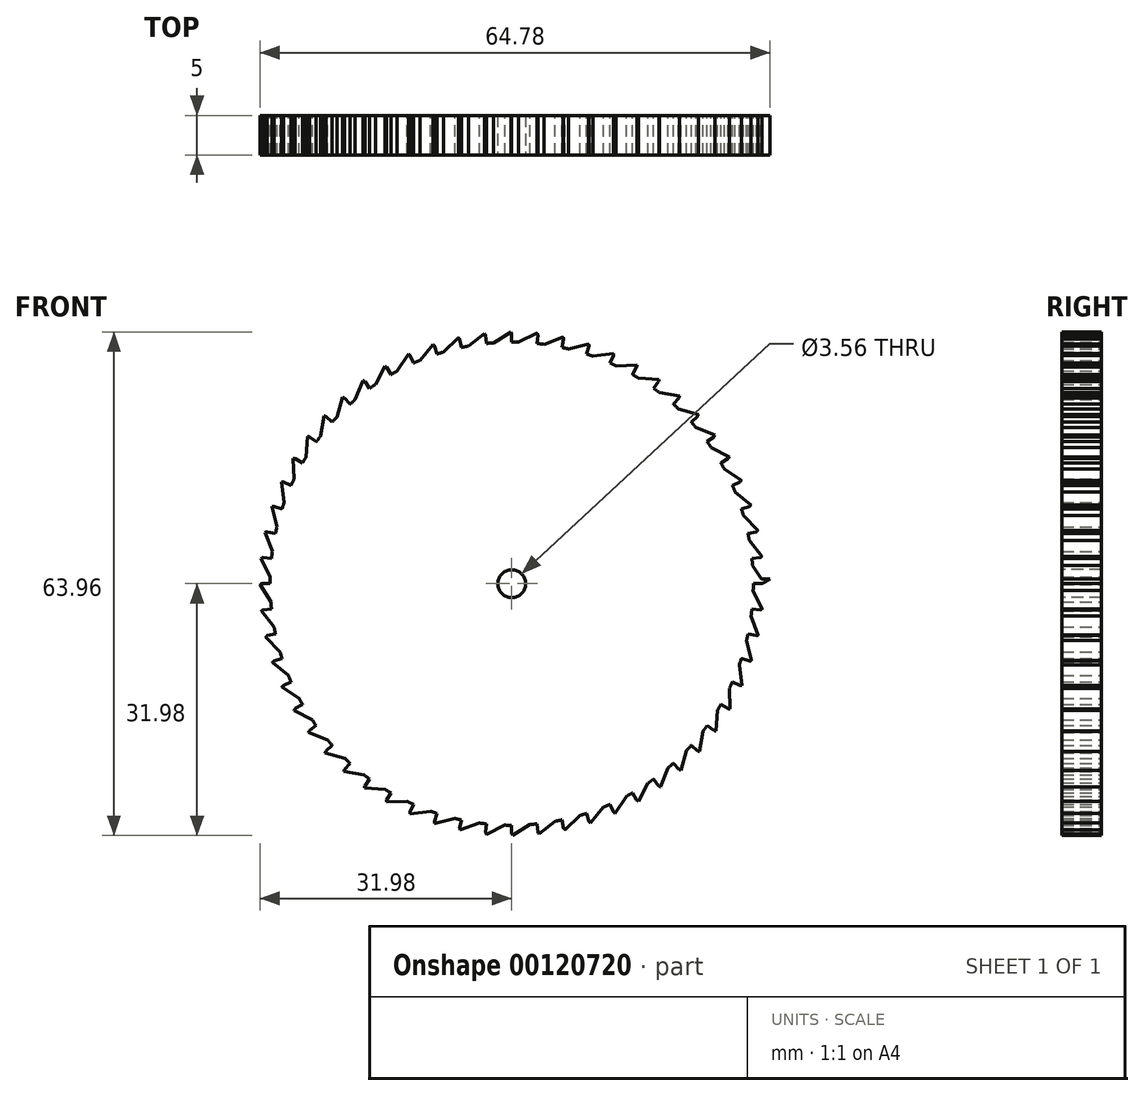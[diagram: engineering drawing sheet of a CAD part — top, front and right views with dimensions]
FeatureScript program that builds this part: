
annotation { "Feature Type Name" : "Feature", "Feature Type Description" : "" }
export const myFeature = defineFeature(function(context is Context, id is Id, definition is map)
    precondition{}
    {
        {
            var Q0;
            Q0=qCreatedBy(makeId("Front.planeOp"),FACE);
            var sketch = newSketch(context, id + "F0", { "sketchPlane" : qUnion([Q0])});
            skArc(sketch, "E0", {"start": v(-7.94, 29.64) * mm, "mid": v(-8.71, 29.42) * mm, "end": v(-9.48, 29.18) * mm});
            skArc(sketch, "E1.trimOffspring", {"start": v(0, 31.75) * mm, "mid": v(-0.28, 32.29) * mm, "end": v(-0.6, 32.8) * mm});
            skLineSegment(sketch, "E2", {"start": v(0, 31.75) * mm, "end": v(0, 30.68) * mm});
            skLineSegment(sketch, "E3", {"start": v(-0.6, 32.8) * mm, "end": v(-0.86, 32.8) * mm});
            skLineSegment(sketch, "E4.MirrorCS", {"start": v(-0.73, 27.19) * mm, "end": v(17.28, 27.8) * mm});
            skArc(sketch, "E5.MirrorCS", {"start": v(-1.66, 31.7) * mm, "mid": v(-1.4, 32.26) * mm, "end": v(-1.12, 32.79) * mm});
            skLineSegment(sketch, "E6.MirrorCS", {"start": v(-1.66, 31.7) * mm, "end": v(-1.6, 30.64) * mm});
            skLineSegment(sketch, "E7.1.0", {"start": v(-4.97, 31.36) * mm, "end": v(-4.8, 30.3) * mm});
            skArc(sketch, "E7.1.1", {"start": v(-4.97, 31.36) * mm, "mid": v(-4.77, 31.93) * mm, "end": v(-4.54, 32.49) * mm});
            skLineSegment(sketch, "E7.1.2", {"start": v(-3.57, 26.96) * mm, "end": v(14.28, 29.45) * mm});
            skLineSegment(sketch, "E7.1.3", {"start": v(-4.03, 32.56) * mm, "end": v(-4.28, 32.52) * mm});
            skArc(sketch, "E7.1.4", {"start": v(-3.32, 31.58) * mm, "mid": v(-3.65, 32.08) * mm, "end": v(-4.03, 32.56) * mm});
            skLineSegment(sketch, "E7.1.5", {"start": v(-3.32, 31.58) * mm, "end": v(-3.2, 30.52) * mm});
            skLineSegment(sketch, "E7.2.0", {"start": v(-8.22, 30.67) * mm, "end": v(-7.94, 29.64) * mm});
            skArc(sketch, "E7.2.1", {"start": v(-8.22, 30.67) * mm, "mid": v(-8.08, 31.26) * mm, "end": v(-7.9, 31.84) * mm});
            skLineSegment(sketch, "E7.2.2", {"start": v(-6.37, 26.44) * mm, "end": v(11.12, 30.78) * mm});
            skLineSegment(sketch, "E7.2.3", {"start": v(-7.4, 31.96) * mm, "end": v(-7.66, 31.9) * mm});
            skArc(sketch, "E7.2.4", {"start": v(-6.6, 31.06) * mm, "mid": v(-6.99, 31.52) * mm, "end": v(-7.4, 31.96) * mm});
            skLineSegment(sketch, "E7.2.5", {"start": v(-6.6, 31.06) * mm, "end": v(-6.38, 30.01) * mm});
            skLineSegment(sketch, "E7.3.0", {"start": v(-11.38, 29.64) * mm, "end": v(-11, 28.65) * mm});
            skArc(sketch, "E7.3.1", {"start": v(-11.38, 29.64) * mm, "mid": v(-11.3, 30.24) * mm, "end": v(-11.2, 30.84) * mm});
            skLineSegment(sketch, "E7.3.2", {"start": v(-9.1, 25.63) * mm, "end": v(7.84, 31.78) * mm});
            skLineSegment(sketch, "E7.3.3", {"start": v(-10.7, 31) * mm, "end": v(-10.95, 30.92) * mm});
            skArc(sketch, "E7.3.4", {"start": v(-9.81, 30.2) * mm, "mid": v(-10.24, 30.62) * mm, "end": v(-10.7, 31) * mm});
            skLineSegment(sketch, "E7.3.5", {"start": v(-9.81, 30.2) * mm, "end": v(-9.48, 29.18) * mm});
            skLineSegment(sketch, "E7.4.0", {"start": v(-14.41, 28.29) * mm, "end": v(-13.93, 27.34) * mm});
            skArc(sketch, "E7.4.1", {"start": v(-14.41, 28.29) * mm, "mid": v(-14.4, 28.9) * mm, "end": v(-14.35, 29.5) * mm});
            skLineSegment(sketch, "E7.4.2", {"start": v(-11.73, 24.54) * mm, "end": v(4.48, 32.42) * mm});
            skLineSegment(sketch, "E7.4.3", {"start": v(-13.9, 29.72) * mm, "end": v(-14.12, 29.6) * mm});
            skArc(sketch, "E7.4.4", {"start": v(-12.91, 29) * mm, "mid": v(-13.39, 29.38) * mm, "end": v(-13.9, 29.72) * mm});
            skLineSegment(sketch, "E7.4.5", {"start": v(-12.91, 29) * mm, "end": v(-12.48, 28.03) * mm});
            skLineSegment(sketch, "E7.5.0", {"start": v(-17.3, 26.63) * mm, "end": v(-16.71, 25.73) * mm});
            skArc(sketch, "E7.5.1", {"start": v(-17.3, 26.63) * mm, "mid": v(-17.35, 27.23) * mm, "end": v(-17.36, 27.84) * mm});
            skLineSegment(sketch, "E7.5.2", {"start": v(-14.23, 23.18) * mm, "end": v(1.07, 32.72) * mm});
            skLineSegment(sketch, "E7.5.3", {"start": v(-16.92, 28.1) * mm, "end": v(-17.14, 27.97) * mm});
            skArc(sketch, "E7.5.4", {"start": v(-15.88, 27.5) * mm, "mid": v(-16.39, 27.82) * mm, "end": v(-16.92, 28.1) * mm});
            skLineSegment(sketch, "E7.5.5", {"start": v(-15.87, 27.5) * mm, "end": v(-15.34, 26.57) * mm});
            skLineSegment(sketch, "E7.6.0", {"start": v(-19.98, 24.67) * mm, "end": v(-19.3, 23.85) * mm});
            skArc(sketch, "E7.6.1", {"start": v(-19.98, 24.67) * mm, "mid": v(-20.1, 25.27) * mm, "end": v(-20.17, 25.87) * mm});
            skLineSegment(sketch, "E7.6.2", {"start": v(-16.57, 21.56) * mm, "end": v(-2.36, 32.65) * mm});
            skLineSegment(sketch, "E7.6.3", {"start": v(-19.77, 26.18) * mm, "end": v(-19.97, 26.03) * mm});
            skArc(sketch, "E7.6.4", {"start": v(-18.66, 25.69) * mm, "mid": v(-19.2, 25.95) * mm, "end": v(-19.77, 26.18) * mm});
            skLineSegment(sketch, "E7.6.5", {"start": v(-18.66, 25.69) * mm, "end": v(-18.04, 24.82) * mm});
            skLineSegment(sketch, "E7.7.0", {"start": v(-22.45, 22.45) * mm, "end": v(-21.7, 21.7) * mm});
            skArc(sketch, "E7.7.1", {"start": v(-22.45, 22.45) * mm, "mid": v(-22.63, 23.03) * mm, "end": v(-22.77, 23.62) * mm});
            skLineSegment(sketch, "E7.7.2", {"start": v(-18.74, 19.71) * mm, "end": v(-5.76, 32.22) * mm});
            skLineSegment(sketch, "E7.7.3", {"start": v(-22.4, 23.97) * mm, "end": v(-22.58, 23.8) * mm});
            skArc(sketch, "E7.7.4", {"start": v(-21.24, 23.6) * mm, "mid": v(-21.81, 23.8) * mm, "end": v(-22.4, 23.97) * mm});
            skLineSegment(sketch, "E7.7.5", {"start": v(-21.24, 23.6) * mm, "end": v(-20.53, 22.8) * mm});
            skLineSegment(sketch, "E7.8.0", {"start": v(-24.67, 19.98) * mm, "end": v(-23.85, 19.3) * mm});
            skArc(sketch, "E7.8.1", {"start": v(-24.67, 19.98) * mm, "mid": v(-24.91, 20.54) * mm, "end": v(-25.11, 21.1) * mm});
            skLineSegment(sketch, "E7.8.2", {"start": v(-20.7, 17.65) * mm, "end": v(-9.1, 31.44) * mm});
            skLineSegment(sketch, "E7.8.3", {"start": v(-24.78, 21.5) * mm, "end": v(-24.95, 21.3) * mm});
            skArc(sketch, "E7.8.4", {"start": v(-23.6, 21.24) * mm, "mid": v(-24.18, 21.4) * mm, "end": v(-24.78, 21.5) * mm});
            skLineSegment(sketch, "E7.8.5", {"start": v(-23.6, 21.24) * mm, "end": v(-22.8, 20.53) * mm});
            skLineSegment(sketch, "E7.9.0", {"start": v(-26.63, 17.3) * mm, "end": v(-25.73, 16.71) * mm});
            skArc(sketch, "E7.9.1", {"start": v(-26.63, 17.3) * mm, "mid": v(-26.92, 17.82) * mm, "end": v(-27.18, 18.37) * mm});
            skLineSegment(sketch, "E7.9.2", {"start": v(-22.43, 15.39) * mm, "end": v(-12.33, 30.32) * mm});
            skLineSegment(sketch, "E7.9.3", {"start": v(-26.89, 18.8) * mm, "end": v(-27.04, 18.58) * mm});
            skArc(sketch, "E7.9.4", {"start": v(-25.69, 18.66) * mm, "mid": v(-26.28, 18.75) * mm, "end": v(-26.89, 18.8) * mm});
            skLineSegment(sketch, "E7.9.5", {"start": v(-25.69, 18.66) * mm, "end": v(-24.82, 18.04) * mm});
            skLineSegment(sketch, "E7.10.0", {"start": v(-28.29, 14.41) * mm, "end": v(-27.34, 13.93) * mm});
            skArc(sketch, "E7.10.1", {"start": v(-28.29, 14.41) * mm, "mid": v(-28.64, 14.9) * mm, "end": v(-28.95, 15.43) * mm});
            skLineSegment(sketch, "E7.10.2", {"start": v(-23.91, 12.96) * mm, "end": v(-15.43, 28.87) * mm});
            skLineSegment(sketch, "E7.10.3", {"start": v(-28.7, 15.88) * mm, "end": v(-28.83, 15.65) * mm});
            skArc(sketch, "E7.10.4", {"start": v(-27.5, 15.88) * mm, "mid": v(-28.1, 15.9) * mm, "end": v(-28.7, 15.88) * mm});
            skLineSegment(sketch, "E7.10.5", {"start": v(-27.5, 15.88) * mm, "end": v(-26.57, 15.34) * mm});
            skLineSegment(sketch, "E7.11.0", {"start": v(-29.64, 11.38) * mm, "end": v(-28.65, 11) * mm});
            skArc(sketch, "E7.11.1", {"start": v(-29.64, 11.38) * mm, "mid": v(-30.04, 11.83) * mm, "end": v(-30.4, 12.32) * mm});
            skLineSegment(sketch, "E7.11.2", {"start": v(-25.13, 10.39) * mm, "end": v(-18.37, 27.1) * mm});
            skLineSegment(sketch, "E7.11.3", {"start": v(-30.2, 12.8) * mm, "end": v(-30.3, 12.55) * mm});
            skArc(sketch, "E7.11.4", {"start": v(-29, 12.91) * mm, "mid": v(-29.6, 12.88) * mm, "end": v(-30.2, 12.8) * mm});
            skLineSegment(sketch, "E7.11.5", {"start": v(-29, 12.91) * mm, "end": v(-28.03, 12.48) * mm});
            skLineSegment(sketch, "E7.12.0", {"start": v(-30.67, 8.22) * mm, "end": v(-29.64, 7.94) * mm});
            skArc(sketch, "E7.12.1", {"start": v(-30.67, 8.22) * mm, "mid": v(-31.11, 8.63) * mm, "end": v(-31.53, 9.07) * mm});
            skLineSegment(sketch, "E7.12.2", {"start": v(-26.08, 7.7) * mm, "end": v(-21.1, 25.03) * mm});
            skLineSegment(sketch, "E7.12.3", {"start": v(-31.38, 9.56) * mm, "end": v(-31.45, 9.32) * mm});
            skArc(sketch, "E7.12.4", {"start": v(-30.2, 9.81) * mm, "mid": v(-30.8, 9.7) * mm, "end": v(-31.38, 9.56) * mm});
            skLineSegment(sketch, "E7.12.5", {"start": v(-30.2, 9.81) * mm, "end": v(-29.18, 9.48) * mm});
            skLineSegment(sketch, "E7.13.0", {"start": v(-31.36, 4.97) * mm, "end": v(-30.3, 4.8) * mm});
            skArc(sketch, "E7.13.1", {"start": v(-31.36, 4.97) * mm, "mid": v(-31.84, 5.33) * mm, "end": v(-32.3, 5.73) * mm});
            skLineSegment(sketch, "E7.13.2", {"start": v(-26.75, 4.93) * mm, "end": v(-23.6, 22.68) * mm});
            skLineSegment(sketch, "E7.13.3", {"start": v(-32.2, 6.23) * mm, "end": v(-32.26, 5.98) * mm});
            skArc(sketch, "E7.13.4", {"start": v(-31.06, 6.6) * mm, "mid": v(-31.64, 6.44) * mm, "end": v(-32.2, 6.23) * mm});
            skLineSegment(sketch, "E7.13.5", {"start": v(-31.06, 6.6) * mm, "end": v(-30.01, 6.38) * mm});
            skLineSegment(sketch, "E7.14.0", {"start": v(-31.7, 1.66) * mm, "end": v(-30.64, 1.6) * mm});
            skArc(sketch, "E7.14.1", {"start": v(-31.7, 1.66) * mm, "mid": v(-32.23, 1.97) * mm, "end": v(-32.72, 2.32) * mm});
            skLineSegment(sketch, "E7.14.2", {"start": v(-27.11, 2.11) * mm, "end": v(-25.84, 20.1) * mm});
            skLineSegment(sketch, "E7.14.3", {"start": v(-32.68, 2.83) * mm, "end": v(-32.7, 2.57) * mm});
            skArc(sketch, "E7.14.4", {"start": v(-31.58, 3.32) * mm, "mid": v(-32.14, 3.1) * mm, "end": v(-32.68, 2.83) * mm});
            skLineSegment(sketch, "E7.14.5", {"start": v(-31.58, 3.32) * mm, "end": v(-30.52, 3.2) * mm});
            skLineSegment(sketch, "E7.15.0", {"start": v(-31.7, -1.66) * mm, "end": v(-30.64, -1.6) * mm});
            skArc(sketch, "E7.15.1", {"start": v(-31.7, -1.66) * mm, "mid": v(-32.26, -1.4) * mm, "end": v(-32.79, -1.12) * mm});
            skLineSegment(sketch, "E7.15.2", {"start": v(-27.19, -0.73) * mm, "end": v(-27.8, 17.28) * mm});
            skLineSegment(sketch, "E7.15.3", {"start": v(-32.8, -0.6) * mm, "end": v(-32.8, -0.86) * mm});
            skArc(sketch, "E7.15.4", {"start": v(-31.75, 0) * mm, "mid": v(-32.29, -0.28) * mm, "end": v(-32.8, -0.6) * mm});
            skLineSegment(sketch, "E7.15.5", {"start": v(-31.75, 0) * mm, "end": v(-30.68, 0) * mm});
            skLineSegment(sketch, "E7.16.0", {"start": v(-31.36, -4.97) * mm, "end": v(-30.3, -4.8) * mm});
            skArc(sketch, "E7.16.1", {"start": v(-31.36, -4.97) * mm, "mid": v(-31.93, -4.77) * mm, "end": v(-32.49, -4.54) * mm});
            skLineSegment(sketch, "E7.16.2", {"start": v(-26.96, -3.57) * mm, "end": v(-29.45, 14.28) * mm});
            skLineSegment(sketch, "E7.16.3", {"start": v(-32.56, -4.03) * mm, "end": v(-32.52, -4.28) * mm});
            skArc(sketch, "E7.16.4", {"start": v(-31.58, -3.32) * mm, "mid": v(-32.08, -3.65) * mm, "end": v(-32.56, -4.03) * mm});
            skLineSegment(sketch, "E7.16.5", {"start": v(-31.58, -3.32) * mm, "end": v(-30.52, -3.2) * mm});
            skLineSegment(sketch, "E7.17.0", {"start": v(-30.67, -8.22) * mm, "end": v(-29.64, -7.94) * mm});
            skArc(sketch, "E7.17.1", {"start": v(-30.67, -8.22) * mm, "mid": v(-31.26, -8.08) * mm, "end": v(-31.84, -7.9) * mm});
            skLineSegment(sketch, "E7.17.2", {"start": v(-26.44, -6.37) * mm, "end": v(-30.78, 11.12) * mm});
            skLineSegment(sketch, "E7.17.3", {"start": v(-31.96, -7.4) * mm, "end": v(-31.9, -7.66) * mm});
            skArc(sketch, "E7.17.4", {"start": v(-31.06, -6.6) * mm, "mid": v(-31.52, -6.99) * mm, "end": v(-31.96, -7.4) * mm});
            skLineSegment(sketch, "E7.17.5", {"start": v(-31.06, -6.6) * mm, "end": v(-30.01, -6.38) * mm});
            skLineSegment(sketch, "E7.18.0", {"start": v(-29.64, -11.38) * mm, "end": v(-28.65, -11) * mm});
            skArc(sketch, "E7.18.1", {"start": v(-29.64, -11.38) * mm, "mid": v(-30.24, -11.3) * mm, "end": v(-30.84, -11.2) * mm});
            skLineSegment(sketch, "E7.18.2", {"start": v(-25.63, -9.1) * mm, "end": v(-31.78, 7.84) * mm});
            skLineSegment(sketch, "E7.18.3", {"start": v(-31, -10.7) * mm, "end": v(-30.92, -10.95) * mm});
            skArc(sketch, "E7.18.4", {"start": v(-30.2, -9.81) * mm, "mid": v(-30.62, -10.24) * mm, "end": v(-31, -10.7) * mm});
            skLineSegment(sketch, "E7.18.5", {"start": v(-30.2, -9.81) * mm, "end": v(-29.18, -9.48) * mm});
            skLineSegment(sketch, "E7.19.0", {"start": v(-28.29, -14.41) * mm, "end": v(-27.34, -13.93) * mm});
            skArc(sketch, "E7.19.1", {"start": v(-28.29, -14.41) * mm, "mid": v(-28.9, -14.4) * mm, "end": v(-29.5, -14.35) * mm});
            skLineSegment(sketch, "E7.19.2", {"start": v(-24.54, -11.73) * mm, "end": v(-32.42, 4.48) * mm});
            skLineSegment(sketch, "E7.19.3", {"start": v(-29.72, -13.9) * mm, "end": v(-29.6, -14.12) * mm});
            skArc(sketch, "E7.19.4", {"start": v(-29, -12.91) * mm, "mid": v(-29.38, -13.39) * mm, "end": v(-29.72, -13.9) * mm});
            skLineSegment(sketch, "E7.19.5", {"start": v(-29, -12.91) * mm, "end": v(-28.03, -12.48) * mm});
            skLineSegment(sketch, "E7.20.0", {"start": v(-26.63, -17.3) * mm, "end": v(-25.73, -16.71) * mm});
            skArc(sketch, "E7.20.1", {"start": v(-26.63, -17.3) * mm, "mid": v(-27.23, -17.35) * mm, "end": v(-27.84, -17.36) * mm});
            skLineSegment(sketch, "E7.20.2", {"start": v(-23.18, -14.23) * mm, "end": v(-32.72, 1.07) * mm});
            skLineSegment(sketch, "E7.20.3", {"start": v(-28.1, -16.92) * mm, "end": v(-27.97, -17.14) * mm});
            skArc(sketch, "E7.20.4", {"start": v(-27.5, -15.87) * mm, "mid": v(-27.82, -16.39) * mm, "end": v(-28.1, -16.92) * mm});
            skLineSegment(sketch, "E7.20.5", {"start": v(-27.5, -15.87) * mm, "end": v(-26.57, -15.34) * mm});
            skLineSegment(sketch, "E7.21.0", {"start": v(-24.67, -19.98) * mm, "end": v(-23.85, -19.3) * mm});
            skArc(sketch, "E7.21.1", {"start": v(-24.67, -19.98) * mm, "mid": v(-25.27, -20.1) * mm, "end": v(-25.87, -20.17) * mm});
            skLineSegment(sketch, "E7.21.2", {"start": v(-21.56, -16.57) * mm, "end": v(-32.65, -2.36) * mm});
            skLineSegment(sketch, "E7.21.3", {"start": v(-26.18, -19.77) * mm, "end": v(-26.03, -19.97) * mm});
            skArc(sketch, "E7.21.4", {"start": v(-25.69, -18.66) * mm, "mid": v(-25.95, -19.2) * mm, "end": v(-26.18, -19.77) * mm});
            skLineSegment(sketch, "E7.21.5", {"start": v(-25.69, -18.66) * mm, "end": v(-24.82, -18.04) * mm});
            skLineSegment(sketch, "E7.22.0", {"start": v(-22.45, -22.45) * mm, "end": v(-21.7, -21.7) * mm});
            skArc(sketch, "E7.22.1", {"start": v(-22.45, -22.45) * mm, "mid": v(-23.03, -22.63) * mm, "end": v(-23.62, -22.77) * mm});
            skLineSegment(sketch, "E7.22.2", {"start": v(-19.71, -18.74) * mm, "end": v(-32.22, -5.76) * mm});
            skLineSegment(sketch, "E7.22.3", {"start": v(-23.97, -22.4) * mm, "end": v(-23.8, -22.58) * mm});
            skArc(sketch, "E7.22.4", {"start": v(-23.6, -21.24) * mm, "mid": v(-23.8, -21.81) * mm, "end": v(-23.97, -22.4) * mm});
            skLineSegment(sketch, "E7.22.5", {"start": v(-23.6, -21.24) * mm, "end": v(-22.8, -20.53) * mm});
            skLineSegment(sketch, "E7.23.0", {"start": v(-19.98, -24.67) * mm, "end": v(-19.3, -23.85) * mm});
            skArc(sketch, "E7.23.1", {"start": v(-19.98, -24.67) * mm, "mid": v(-20.54, -24.91) * mm, "end": v(-21.1, -25.11) * mm});
            skLineSegment(sketch, "E7.23.2", {"start": v(-17.65, -20.7) * mm, "end": v(-31.44, -9.1) * mm});
            skLineSegment(sketch, "E7.23.3", {"start": v(-21.5, -24.78) * mm, "end": v(-21.3, -24.95) * mm});
            skArc(sketch, "E7.23.4", {"start": v(-21.24, -23.6) * mm, "mid": v(-21.4, -24.18) * mm, "end": v(-21.5, -24.78) * mm});
            skLineSegment(sketch, "E7.23.5", {"start": v(-21.24, -23.6) * mm, "end": v(-20.53, -22.8) * mm});
            skLineSegment(sketch, "E7.24.0", {"start": v(-17.3, -26.63) * mm, "end": v(-16.71, -25.73) * mm});
            skArc(sketch, "E7.24.1", {"start": v(-17.3, -26.63) * mm, "mid": v(-17.82, -26.92) * mm, "end": v(-18.37, -27.18) * mm});
            skLineSegment(sketch, "E7.24.2", {"start": v(-15.39, -22.43) * mm, "end": v(-30.32, -12.33) * mm});
            skLineSegment(sketch, "E7.24.3", {"start": v(-18.8, -26.89) * mm, "end": v(-18.58, -27.04) * mm});
            skArc(sketch, "E7.24.4", {"start": v(-18.66, -25.69) * mm, "mid": v(-18.75, -26.28) * mm, "end": v(-18.8, -26.89) * mm});
            skLineSegment(sketch, "E7.24.5", {"start": v(-18.66, -25.69) * mm, "end": v(-18.04, -24.82) * mm});
            skLineSegment(sketch, "E7.25.0", {"start": v(-14.41, -28.29) * mm, "end": v(-13.93, -27.34) * mm});
            skArc(sketch, "E7.25.1", {"start": v(-14.41, -28.29) * mm, "mid": v(-14.9, -28.64) * mm, "end": v(-15.43, -28.95) * mm});
            skLineSegment(sketch, "E7.25.2", {"start": v(-12.96, -23.91) * mm, "end": v(-28.87, -15.43) * mm});
            skLineSegment(sketch, "E7.25.3", {"start": v(-15.88, -28.7) * mm, "end": v(-15.65, -28.83) * mm});
            skArc(sketch, "E7.25.4", {"start": v(-15.88, -27.5) * mm, "mid": v(-15.9, -28.1) * mm, "end": v(-15.88, -28.7) * mm});
            skLineSegment(sketch, "E7.25.5", {"start": v(-15.87, -27.5) * mm, "end": v(-15.34, -26.57) * mm});
            skLineSegment(sketch, "E7.26.0", {"start": v(-11.38, -29.64) * mm, "end": v(-11, -28.65) * mm});
            skArc(sketch, "E7.26.1", {"start": v(-11.38, -29.64) * mm, "mid": v(-11.83, -30.04) * mm, "end": v(-12.32, -30.4) * mm});
            skLineSegment(sketch, "E7.26.2", {"start": v(-10.39, -25.13) * mm, "end": v(-27.1, -18.37) * mm});
            skLineSegment(sketch, "E7.26.3", {"start": v(-12.8, -30.2) * mm, "end": v(-12.55, -30.3) * mm});
            skArc(sketch, "E7.26.4", {"start": v(-12.91, -29) * mm, "mid": v(-12.88, -29.6) * mm, "end": v(-12.8, -30.2) * mm});
            skLineSegment(sketch, "E7.26.5", {"start": v(-12.91, -29) * mm, "end": v(-12.48, -28.03) * mm});
            skLineSegment(sketch, "E7.27.0", {"start": v(-8.22, -30.67) * mm, "end": v(-7.94, -29.64) * mm});
            skArc(sketch, "E7.27.1", {"start": v(-8.22, -30.67) * mm, "mid": v(-8.63, -31.11) * mm, "end": v(-9.07, -31.53) * mm});
            skLineSegment(sketch, "E7.27.2", {"start": v(-7.7, -26.08) * mm, "end": v(-25.03, -21.1) * mm});
            skLineSegment(sketch, "E7.27.3", {"start": v(-9.56, -31.38) * mm, "end": v(-9.32, -31.45) * mm});
            skArc(sketch, "E7.27.4", {"start": v(-9.81, -30.2) * mm, "mid": v(-9.7, -30.8) * mm, "end": v(-9.56, -31.38) * mm});
            skLineSegment(sketch, "E7.27.5", {"start": v(-9.81, -30.2) * mm, "end": v(-9.48, -29.18) * mm});
            skLineSegment(sketch, "E7.28.0", {"start": v(-4.97, -31.36) * mm, "end": v(-4.8, -30.3) * mm});
            skArc(sketch, "E7.28.1", {"start": v(-4.97, -31.36) * mm, "mid": v(-5.33, -31.84) * mm, "end": v(-5.73, -32.3) * mm});
            skLineSegment(sketch, "E7.28.2", {"start": v(-4.93, -26.75) * mm, "end": v(-22.68, -23.6) * mm});
            skLineSegment(sketch, "E7.28.3", {"start": v(-6.23, -32.2) * mm, "end": v(-5.98, -32.26) * mm});
            skArc(sketch, "E7.28.4", {"start": v(-6.6, -31.06) * mm, "mid": v(-6.44, -31.64) * mm, "end": v(-6.23, -32.2) * mm});
            skLineSegment(sketch, "E7.28.5", {"start": v(-6.6, -31.06) * mm, "end": v(-6.38, -30.01) * mm});
            skLineSegment(sketch, "E7.29.0", {"start": v(-1.66, -31.7) * mm, "end": v(-1.6, -30.64) * mm});
            skArc(sketch, "E7.29.1", {"start": v(-1.66, -31.7) * mm, "mid": v(-1.97, -32.23) * mm, "end": v(-2.32, -32.72) * mm});
            skLineSegment(sketch, "E7.29.2", {"start": v(-2.11, -27.11) * mm, "end": v(-20.1, -25.84) * mm});
            skLineSegment(sketch, "E7.29.3", {"start": v(-2.83, -32.68) * mm, "end": v(-2.57, -32.7) * mm});
            skArc(sketch, "E7.29.4", {"start": v(-3.32, -31.58) * mm, "mid": v(-3.1, -32.14) * mm, "end": v(-2.83, -32.68) * mm});
            skLineSegment(sketch, "E7.29.5", {"start": v(-3.32, -31.58) * mm, "end": v(-3.2, -30.52) * mm});
            skLineSegment(sketch, "E7.30.0", {"start": v(1.66, -31.7) * mm, "end": v(1.6, -30.64) * mm});
            skArc(sketch, "E7.30.1", {"start": v(1.66, -31.7) * mm, "mid": v(1.4, -32.26) * mm, "end": v(1.12, -32.79) * mm});
            skLineSegment(sketch, "E7.30.2", {"start": v(0.73, -27.19) * mm, "end": v(-17.28, -27.8) * mm});
            skLineSegment(sketch, "E7.30.3", {"start": v(0.6, -32.8) * mm, "end": v(0.86, -32.8) * mm});
            skArc(sketch, "E7.30.4", {"start": v(0, -31.75) * mm, "mid": v(0.28, -32.29) * mm, "end": v(0.6, -32.8) * mm});
            skLineSegment(sketch, "E7.30.5", {"start": v(0, -31.75) * mm, "end": v(0, -30.68) * mm});
            skLineSegment(sketch, "E7.31.0", {"start": v(4.97, -31.36) * mm, "end": v(4.8, -30.3) * mm});
            skArc(sketch, "E7.31.1", {"start": v(4.97, -31.36) * mm, "mid": v(4.77, -31.93) * mm, "end": v(4.54, -32.49) * mm});
            skLineSegment(sketch, "E7.31.2", {"start": v(3.57, -26.96) * mm, "end": v(-14.28, -29.45) * mm});
            skLineSegment(sketch, "E7.31.3", {"start": v(4.03, -32.56) * mm, "end": v(4.28, -32.52) * mm});
            skArc(sketch, "E7.31.4", {"start": v(3.32, -31.58) * mm, "mid": v(3.65, -32.08) * mm, "end": v(4.03, -32.56) * mm});
            skLineSegment(sketch, "E7.31.5", {"start": v(3.32, -31.58) * mm, "end": v(3.2, -30.52) * mm});
            skLineSegment(sketch, "E7.32.0", {"start": v(8.22, -30.67) * mm, "end": v(7.94, -29.64) * mm});
            skArc(sketch, "E7.32.1", {"start": v(8.22, -30.67) * mm, "mid": v(8.08, -31.26) * mm, "end": v(7.9, -31.84) * mm});
            skLineSegment(sketch, "E7.32.2", {"start": v(6.37, -26.44) * mm, "end": v(-11.12, -30.78) * mm});
            skLineSegment(sketch, "E7.32.3", {"start": v(7.4, -31.96) * mm, "end": v(7.66, -31.9) * mm});
            skArc(sketch, "E7.32.4", {"start": v(6.6, -31.06) * mm, "mid": v(6.99, -31.52) * mm, "end": v(7.4, -31.96) * mm});
            skLineSegment(sketch, "E7.32.5", {"start": v(6.6, -31.06) * mm, "end": v(6.38, -30.01) * mm});
            skLineSegment(sketch, "E7.33.0", {"start": v(11.38, -29.64) * mm, "end": v(11, -28.65) * mm});
            skArc(sketch, "E7.33.1", {"start": v(11.38, -29.64) * mm, "mid": v(11.3, -30.24) * mm, "end": v(11.2, -30.84) * mm});
            skLineSegment(sketch, "E7.33.2", {"start": v(9.1, -25.63) * mm, "end": v(-7.84, -31.78) * mm});
            skLineSegment(sketch, "E7.33.3", {"start": v(10.7, -31) * mm, "end": v(10.95, -30.92) * mm});
            skArc(sketch, "E7.33.4", {"start": v(9.81, -30.2) * mm, "mid": v(10.24, -30.62) * mm, "end": v(10.7, -31) * mm});
            skLineSegment(sketch, "E7.33.5", {"start": v(9.81, -30.2) * mm, "end": v(9.48, -29.18) * mm});
            skLineSegment(sketch, "E7.34.0", {"start": v(14.41, -28.29) * mm, "end": v(13.93, -27.34) * mm});
            skArc(sketch, "E7.34.1", {"start": v(14.41, -28.29) * mm, "mid": v(14.4, -28.9) * mm, "end": v(14.35, -29.5) * mm});
            skLineSegment(sketch, "E7.34.2", {"start": v(11.73, -24.54) * mm, "end": v(-4.48, -32.42) * mm});
            skLineSegment(sketch, "E7.34.3", {"start": v(13.9, -29.72) * mm, "end": v(14.12, -29.6) * mm});
            skArc(sketch, "E7.34.4", {"start": v(12.91, -29) * mm, "mid": v(13.39, -29.38) * mm, "end": v(13.9, -29.72) * mm});
            skLineSegment(sketch, "E7.34.5", {"start": v(12.91, -29) * mm, "end": v(12.48, -28.03) * mm});
            skLineSegment(sketch, "E7.35.0", {"start": v(17.3, -26.63) * mm, "end": v(16.71, -25.73) * mm});
            skArc(sketch, "E7.35.1", {"start": v(17.3, -26.63) * mm, "mid": v(17.35, -27.23) * mm, "end": v(17.36, -27.84) * mm});
            skLineSegment(sketch, "E7.35.2", {"start": v(14.23, -23.18) * mm, "end": v(-1.07, -32.72) * mm});
            skLineSegment(sketch, "E7.35.3", {"start": v(16.92, -28.1) * mm, "end": v(17.14, -27.97) * mm});
            skArc(sketch, "E7.35.4", {"start": v(15.87, -27.5) * mm, "mid": v(16.39, -27.82) * mm, "end": v(16.92, -28.1) * mm});
            skLineSegment(sketch, "E7.35.5", {"start": v(15.87, -27.5) * mm, "end": v(15.34, -26.57) * mm});
            skLineSegment(sketch, "E7.36.0", {"start": v(19.98, -24.67) * mm, "end": v(19.3, -23.85) * mm});
            skArc(sketch, "E7.36.1", {"start": v(19.98, -24.67) * mm, "mid": v(20.1, -25.27) * mm, "end": v(20.17, -25.87) * mm});
            skLineSegment(sketch, "E7.36.2", {"start": v(16.57, -21.56) * mm, "end": v(2.36, -32.65) * mm});
            skLineSegment(sketch, "E7.36.3", {"start": v(19.77, -26.18) * mm, "end": v(19.97, -26.03) * mm});
            skArc(sketch, "E7.36.4", {"start": v(18.66, -25.69) * mm, "mid": v(19.2, -25.95) * mm, "end": v(19.77, -26.18) * mm});
            skLineSegment(sketch, "E7.36.5", {"start": v(18.66, -25.69) * mm, "end": v(18.04, -24.82) * mm});
            skLineSegment(sketch, "E7.37.0", {"start": v(22.45, -22.45) * mm, "end": v(21.7, -21.7) * mm});
            skArc(sketch, "E7.37.1", {"start": v(22.45, -22.45) * mm, "mid": v(22.63, -23.03) * mm, "end": v(22.77, -23.62) * mm});
            skLineSegment(sketch, "E7.37.2", {"start": v(18.74, -19.71) * mm, "end": v(5.76, -32.22) * mm});
            skLineSegment(sketch, "E7.37.3", {"start": v(22.4, -23.97) * mm, "end": v(22.58, -23.8) * mm});
            skArc(sketch, "E7.37.4", {"start": v(21.24, -23.6) * mm, "mid": v(21.81, -23.8) * mm, "end": v(22.4, -23.97) * mm});
            skLineSegment(sketch, "E7.37.5", {"start": v(21.24, -23.6) * mm, "end": v(20.53, -22.8) * mm});
            skLineSegment(sketch, "E7.38.0", {"start": v(24.67, -19.98) * mm, "end": v(23.85, -19.3) * mm});
            skArc(sketch, "E7.38.1", {"start": v(24.67, -19.98) * mm, "mid": v(24.91, -20.54) * mm, "end": v(25.11, -21.1) * mm});
            skLineSegment(sketch, "E7.38.2", {"start": v(20.7, -17.65) * mm, "end": v(9.1, -31.44) * mm});
            skLineSegment(sketch, "E7.38.3", {"start": v(24.78, -21.5) * mm, "end": v(24.95, -21.3) * mm});
            skArc(sketch, "E7.38.4", {"start": v(23.6, -21.24) * mm, "mid": v(24.18, -21.4) * mm, "end": v(24.78, -21.5) * mm});
            skLineSegment(sketch, "E7.38.5", {"start": v(23.6, -21.24) * mm, "end": v(22.8, -20.53) * mm});
            skLineSegment(sketch, "E7.39.0", {"start": v(26.63, -17.3) * mm, "end": v(25.73, -16.71) * mm});
            skArc(sketch, "E7.39.1", {"start": v(26.63, -17.3) * mm, "mid": v(26.92, -17.82) * mm, "end": v(27.18, -18.37) * mm});
            skLineSegment(sketch, "E7.39.2", {"start": v(22.43, -15.39) * mm, "end": v(12.33, -30.32) * mm});
            skLineSegment(sketch, "E7.39.3", {"start": v(26.89, -18.8) * mm, "end": v(27.04, -18.58) * mm});
            skArc(sketch, "E7.39.4", {"start": v(25.69, -18.66) * mm, "mid": v(26.28, -18.75) * mm, "end": v(26.89, -18.8) * mm});
            skLineSegment(sketch, "E7.39.5", {"start": v(25.69, -18.66) * mm, "end": v(24.82, -18.04) * mm});
            skLineSegment(sketch, "E7.40.0", {"start": v(28.29, -14.41) * mm, "end": v(27.34, -13.93) * mm});
            skArc(sketch, "E7.40.1", {"start": v(28.29, -14.41) * mm, "mid": v(28.64, -14.9) * mm, "end": v(28.95, -15.43) * mm});
            skLineSegment(sketch, "E7.40.2", {"start": v(23.91, -12.96) * mm, "end": v(15.43, -28.87) * mm});
            skLineSegment(sketch, "E7.40.3", {"start": v(28.7, -15.88) * mm, "end": v(28.83, -15.65) * mm});
            skArc(sketch, "E7.40.4", {"start": v(27.5, -15.88) * mm, "mid": v(28.1, -15.9) * mm, "end": v(28.7, -15.88) * mm});
            skLineSegment(sketch, "E7.40.5", {"start": v(27.5, -15.88) * mm, "end": v(26.57, -15.34) * mm});
            skLineSegment(sketch, "E7.41.0", {"start": v(29.64, -11.38) * mm, "end": v(28.65, -11) * mm});
            skArc(sketch, "E7.41.1", {"start": v(29.64, -11.38) * mm, "mid": v(30.04, -11.83) * mm, "end": v(30.4, -12.32) * mm});
            skLineSegment(sketch, "E7.41.2", {"start": v(25.13, -10.39) * mm, "end": v(18.37, -27.1) * mm});
            skLineSegment(sketch, "E7.41.3", {"start": v(30.2, -12.8) * mm, "end": v(30.3, -12.55) * mm});
            skArc(sketch, "E7.41.4", {"start": v(29, -12.91) * mm, "mid": v(29.6, -12.88) * mm, "end": v(30.2, -12.8) * mm});
            skLineSegment(sketch, "E7.41.5", {"start": v(29, -12.91) * mm, "end": v(28.03, -12.48) * mm});
            skLineSegment(sketch, "E7.42.0", {"start": v(30.67, -8.22) * mm, "end": v(29.64, -7.94) * mm});
            skArc(sketch, "E7.42.1", {"start": v(30.67, -8.22) * mm, "mid": v(31.11, -8.63) * mm, "end": v(31.53, -9.07) * mm});
            skLineSegment(sketch, "E7.42.2", {"start": v(26.08, -7.7) * mm, "end": v(21.1, -25.03) * mm});
            skLineSegment(sketch, "E7.42.3", {"start": v(31.38, -9.56) * mm, "end": v(31.45, -9.32) * mm});
            skArc(sketch, "E7.42.4", {"start": v(30.2, -9.81) * mm, "mid": v(30.8, -9.7) * mm, "end": v(31.38, -9.56) * mm});
            skLineSegment(sketch, "E7.42.5", {"start": v(30.2, -9.81) * mm, "end": v(29.18, -9.48) * mm});
            skLineSegment(sketch, "E7.43.0", {"start": v(31.36, -4.97) * mm, "end": v(30.3, -4.8) * mm});
            skArc(sketch, "E7.43.1", {"start": v(31.36, -4.97) * mm, "mid": v(31.84, -5.33) * mm, "end": v(32.3, -5.73) * mm});
            skLineSegment(sketch, "E7.43.2", {"start": v(26.75, -4.93) * mm, "end": v(23.6, -22.68) * mm});
            skLineSegment(sketch, "E7.43.3", {"start": v(32.2, -6.23) * mm, "end": v(32.26, -5.98) * mm});
            skArc(sketch, "E7.43.4", {"start": v(31.06, -6.6) * mm, "mid": v(31.64, -6.44) * mm, "end": v(32.2, -6.23) * mm});
            skLineSegment(sketch, "E7.43.5", {"start": v(31.06, -6.6) * mm, "end": v(30.01, -6.38) * mm});
            skLineSegment(sketch, "E7.44.0", {"start": v(31.7, -1.66) * mm, "end": v(30.64, -1.6) * mm});
            skArc(sketch, "E7.44.1", {"start": v(31.7, -1.66) * mm, "mid": v(32.23, -1.97) * mm, "end": v(32.72, -2.32) * mm});
            skLineSegment(sketch, "E7.44.2", {"start": v(27.11, -2.11) * mm, "end": v(25.84, -20.1) * mm});
            skLineSegment(sketch, "E7.44.3", {"start": v(32.68, -2.83) * mm, "end": v(32.7, -2.57) * mm});
            skArc(sketch, "E7.44.4", {"start": v(31.58, -3.32) * mm, "mid": v(32.14, -3.1) * mm, "end": v(32.68, -2.83) * mm});
            skLineSegment(sketch, "E7.44.5", {"start": v(31.58, -3.32) * mm, "end": v(30.52, -3.2) * mm});
            skLineSegment(sketch, "E7.45.0", {"start": v(31.7, 1.66) * mm, "end": v(30.64, 1.6) * mm});
            skArc(sketch, "E7.45.1", {"start": v(31.7, 1.66) * mm, "mid": v(32.26, 1.4) * mm, "end": v(32.79, 1.12) * mm});
            skLineSegment(sketch, "E7.45.2", {"start": v(27.19, 0.73) * mm, "end": v(27.8, -17.28) * mm});
            skLineSegment(sketch, "E7.45.3", {"start": v(32.8, 0.6) * mm, "end": v(32.8, 0.86) * mm});
            skArc(sketch, "E7.45.4", {"start": v(31.75, 0) * mm, "mid": v(32.29, 0.28) * mm, "end": v(32.8, 0.6) * mm});
            skLineSegment(sketch, "E7.45.5", {"start": v(31.75, 0) * mm, "end": v(30.68, 0) * mm});
            skLineSegment(sketch, "E7.46.0", {"start": v(31.36, 4.97) * mm, "end": v(30.3, 4.8) * mm});
            skArc(sketch, "E7.46.1", {"start": v(31.36, 4.97) * mm, "mid": v(31.93, 4.77) * mm, "end": v(32.49, 4.54) * mm});
            skLineSegment(sketch, "E7.46.2", {"start": v(26.96, 3.57) * mm, "end": v(29.45, -14.28) * mm});
            skLineSegment(sketch, "E7.46.3", {"start": v(32.56, 4.03) * mm, "end": v(32.52, 4.28) * mm});
            skArc(sketch, "E7.46.4", {"start": v(31.58, 3.32) * mm, "mid": v(32.08, 3.65) * mm, "end": v(32.56, 4.03) * mm});
            skLineSegment(sketch, "E7.46.5", {"start": v(31.58, 3.32) * mm, "end": v(30.52, 3.2) * mm});
            skLineSegment(sketch, "E7.47.0", {"start": v(30.67, 8.22) * mm, "end": v(29.64, 7.94) * mm});
            skArc(sketch, "E7.47.1", {"start": v(30.67, 8.22) * mm, "mid": v(31.26, 8.08) * mm, "end": v(31.84, 7.9) * mm});
            skLineSegment(sketch, "E7.47.2", {"start": v(26.44, 6.37) * mm, "end": v(30.78, -11.12) * mm});
            skLineSegment(sketch, "E7.47.3", {"start": v(31.96, 7.4) * mm, "end": v(31.9, 7.66) * mm});
            skArc(sketch, "E7.47.4", {"start": v(31.06, 6.6) * mm, "mid": v(31.52, 6.99) * mm, "end": v(31.96, 7.4) * mm});
            skLineSegment(sketch, "E7.47.5", {"start": v(31.06, 6.6) * mm, "end": v(30.01, 6.38) * mm});
            skLineSegment(sketch, "E7.48.0", {"start": v(29.64, 11.38) * mm, "end": v(28.65, 11) * mm});
            skArc(sketch, "E7.48.1", {"start": v(29.64, 11.38) * mm, "mid": v(30.24, 11.3) * mm, "end": v(30.84, 11.2) * mm});
            skLineSegment(sketch, "E7.48.2", {"start": v(25.63, 9.1) * mm, "end": v(31.78, -7.84) * mm});
            skLineSegment(sketch, "E7.48.3", {"start": v(31, 10.7) * mm, "end": v(30.92, 10.95) * mm});
            skArc(sketch, "E7.48.4", {"start": v(30.2, 9.81) * mm, "mid": v(30.62, 10.24) * mm, "end": v(31, 10.7) * mm});
            skLineSegment(sketch, "E7.48.5", {"start": v(30.2, 9.81) * mm, "end": v(29.18, 9.48) * mm});
            skLineSegment(sketch, "E7.49.0", {"start": v(28.29, 14.41) * mm, "end": v(27.34, 13.93) * mm});
            skArc(sketch, "E7.49.1", {"start": v(28.29, 14.41) * mm, "mid": v(28.9, 14.4) * mm, "end": v(29.5, 14.35) * mm});
            skLineSegment(sketch, "E7.49.2", {"start": v(24.54, 11.73) * mm, "end": v(32.42, -4.48) * mm});
            skLineSegment(sketch, "E7.49.3", {"start": v(29.72, 13.9) * mm, "end": v(29.6, 14.12) * mm});
            skArc(sketch, "E7.49.4", {"start": v(29, 12.91) * mm, "mid": v(29.38, 13.39) * mm, "end": v(29.72, 13.9) * mm});
            skLineSegment(sketch, "E7.49.5", {"start": v(29, 12.91) * mm, "end": v(28.03, 12.48) * mm});
            skLineSegment(sketch, "E7.50.0", {"start": v(26.63, 17.3) * mm, "end": v(25.73, 16.71) * mm});
            skArc(sketch, "E7.50.1", {"start": v(26.63, 17.3) * mm, "mid": v(27.23, 17.35) * mm, "end": v(27.84, 17.36) * mm});
            skLineSegment(sketch, "E7.50.2", {"start": v(23.18, 14.23) * mm, "end": v(32.72, -1.07) * mm});
            skLineSegment(sketch, "E7.50.3", {"start": v(28.1, 16.92) * mm, "end": v(27.97, 17.14) * mm});
            skArc(sketch, "E7.50.4", {"start": v(27.5, 15.88) * mm, "mid": v(27.82, 16.39) * mm, "end": v(28.1, 16.92) * mm});
            skLineSegment(sketch, "E7.50.5", {"start": v(27.5, 15.88) * mm, "end": v(26.57, 15.34) * mm});
            skLineSegment(sketch, "E7.51.0", {"start": v(24.67, 19.98) * mm, "end": v(23.85, 19.3) * mm});
            skArc(sketch, "E7.51.1", {"start": v(24.67, 19.98) * mm, "mid": v(25.27, 20.1) * mm, "end": v(25.87, 20.17) * mm});
            skLineSegment(sketch, "E7.51.2", {"start": v(21.56, 16.57) * mm, "end": v(32.65, 2.36) * mm});
            skLineSegment(sketch, "E7.51.3", {"start": v(26.18, 19.77) * mm, "end": v(26.03, 19.97) * mm});
            skArc(sketch, "E7.51.4", {"start": v(25.69, 18.66) * mm, "mid": v(25.95, 19.2) * mm, "end": v(26.18, 19.77) * mm});
            skLineSegment(sketch, "E7.51.5", {"start": v(25.69, 18.66) * mm, "end": v(24.82, 18.04) * mm});
            skLineSegment(sketch, "E7.52.0", {"start": v(22.45, 22.45) * mm, "end": v(21.7, 21.7) * mm});
            skArc(sketch, "E7.52.1", {"start": v(22.45, 22.45) * mm, "mid": v(23.03, 22.63) * mm, "end": v(23.62, 22.77) * mm});
            skLineSegment(sketch, "E7.52.2", {"start": v(19.71, 18.74) * mm, "end": v(32.22, 5.76) * mm});
            skLineSegment(sketch, "E7.52.3", {"start": v(23.97, 22.4) * mm, "end": v(23.8, 22.58) * mm});
            skArc(sketch, "E7.52.4", {"start": v(23.6, 21.24) * mm, "mid": v(23.8, 21.81) * mm, "end": v(23.97, 22.4) * mm});
            skLineSegment(sketch, "E7.52.5", {"start": v(23.6, 21.24) * mm, "end": v(22.8, 20.53) * mm});
            skLineSegment(sketch, "E7.53.0", {"start": v(19.98, 24.67) * mm, "end": v(19.3, 23.85) * mm});
            skArc(sketch, "E7.53.1", {"start": v(19.98, 24.67) * mm, "mid": v(20.54, 24.91) * mm, "end": v(21.1, 25.11) * mm});
            skLineSegment(sketch, "E7.53.2", {"start": v(17.65, 20.7) * mm, "end": v(31.44, 9.1) * mm});
            skLineSegment(sketch, "E7.53.3", {"start": v(21.5, 24.78) * mm, "end": v(21.3, 24.95) * mm});
            skArc(sketch, "E7.53.4", {"start": v(21.24, 23.6) * mm, "mid": v(21.4, 24.18) * mm, "end": v(21.5, 24.78) * mm});
            skLineSegment(sketch, "E7.53.5", {"start": v(21.24, 23.6) * mm, "end": v(20.53, 22.8) * mm});
            skLineSegment(sketch, "E7.54.0", {"start": v(17.3, 26.63) * mm, "end": v(16.71, 25.73) * mm});
            skArc(sketch, "E7.54.1", {"start": v(17.3, 26.63) * mm, "mid": v(17.82, 26.92) * mm, "end": v(18.37, 27.18) * mm});
            skLineSegment(sketch, "E7.54.2", {"start": v(15.39, 22.43) * mm, "end": v(30.32, 12.33) * mm});
            skLineSegment(sketch, "E7.54.3", {"start": v(18.8, 26.89) * mm, "end": v(18.58, 27.04) * mm});
            skArc(sketch, "E7.54.4", {"start": v(18.66, 25.69) * mm, "mid": v(18.75, 26.28) * mm, "end": v(18.8, 26.89) * mm});
            skLineSegment(sketch, "E7.54.5", {"start": v(18.66, 25.69) * mm, "end": v(18.04, 24.82) * mm});
            skLineSegment(sketch, "E7.55.0", {"start": v(14.41, 28.29) * mm, "end": v(13.93, 27.34) * mm});
            skArc(sketch, "E7.55.1", {"start": v(14.41, 28.29) * mm, "mid": v(14.9, 28.64) * mm, "end": v(15.43, 28.95) * mm});
            skLineSegment(sketch, "E7.55.2", {"start": v(12.96, 23.91) * mm, "end": v(28.87, 15.43) * mm});
            skLineSegment(sketch, "E7.55.3", {"start": v(15.88, 28.7) * mm, "end": v(15.65, 28.83) * mm});
            skArc(sketch, "E7.55.4", {"start": v(15.87, 27.5) * mm, "mid": v(15.9, 28.1) * mm, "end": v(15.88, 28.7) * mm});
            skLineSegment(sketch, "E7.55.5", {"start": v(15.87, 27.5) * mm, "end": v(15.34, 26.57) * mm});
            skLineSegment(sketch, "E7.56.0", {"start": v(11.38, 29.64) * mm, "end": v(11, 28.65) * mm});
            skArc(sketch, "E7.56.1", {"start": v(11.38, 29.64) * mm, "mid": v(11.83, 30.04) * mm, "end": v(12.32, 30.4) * mm});
            skLineSegment(sketch, "E7.56.2", {"start": v(10.39, 25.13) * mm, "end": v(27.1, 18.37) * mm});
            skLineSegment(sketch, "E7.56.3", {"start": v(12.8, 30.2) * mm, "end": v(12.55, 30.3) * mm});
            skArc(sketch, "E7.56.4", {"start": v(12.91, 29) * mm, "mid": v(12.88, 29.6) * mm, "end": v(12.8, 30.2) * mm});
            skLineSegment(sketch, "E7.56.5", {"start": v(12.91, 29) * mm, "end": v(12.48, 28.03) * mm});
            skLineSegment(sketch, "E7.57.0", {"start": v(8.22, 30.67) * mm, "end": v(7.94, 29.64) * mm});
            skArc(sketch, "E7.57.1", {"start": v(8.22, 30.67) * mm, "mid": v(8.63, 31.11) * mm, "end": v(9.07, 31.53) * mm});
            skLineSegment(sketch, "E7.57.2", {"start": v(7.7, 26.08) * mm, "end": v(25.03, 21.1) * mm});
            skLineSegment(sketch, "E7.57.3", {"start": v(9.56, 31.38) * mm, "end": v(9.32, 31.45) * mm});
            skArc(sketch, "E7.57.4", {"start": v(9.81, 30.2) * mm, "mid": v(9.7, 30.8) * mm, "end": v(9.56, 31.38) * mm});
            skLineSegment(sketch, "E7.57.5", {"start": v(9.81, 30.2) * mm, "end": v(9.48, 29.18) * mm});
            skLineSegment(sketch, "E7.58.0", {"start": v(4.97, 31.36) * mm, "end": v(4.8, 30.3) * mm});
            skArc(sketch, "E7.58.1", {"start": v(4.97, 31.36) * mm, "mid": v(5.33, 31.84) * mm, "end": v(5.73, 32.3) * mm});
            skLineSegment(sketch, "E7.58.2", {"start": v(4.93, 26.75) * mm, "end": v(22.68, 23.6) * mm});
            skLineSegment(sketch, "E7.58.3", {"start": v(6.23, 32.2) * mm, "end": v(5.98, 32.26) * mm});
            skArc(sketch, "E7.58.4", {"start": v(6.6, 31.06) * mm, "mid": v(6.44, 31.64) * mm, "end": v(6.23, 32.2) * mm});
            skLineSegment(sketch, "E7.58.5", {"start": v(6.6, 31.06) * mm, "end": v(6.38, 30.01) * mm});
            skLineSegment(sketch, "E7.59.0", {"start": v(1.66, 31.7) * mm, "end": v(1.6, 30.64) * mm});
            skArc(sketch, "E7.59.1", {"start": v(1.66, 31.7) * mm, "mid": v(1.97, 32.23) * mm, "end": v(2.32, 32.72) * mm});
            skLineSegment(sketch, "E7.59.2", {"start": v(2.11, 27.11) * mm, "end": v(20.1, 25.84) * mm});
            skLineSegment(sketch, "E7.59.3", {"start": v(2.83, 32.68) * mm, "end": v(2.57, 32.7) * mm});
            skArc(sketch, "E7.59.4", {"start": v(3.32, 31.58) * mm, "mid": v(3.1, 32.14) * mm, "end": v(2.83, 32.68) * mm});
            skLineSegment(sketch, "E7.59.5", {"start": v(3.32, 31.58) * mm, "end": v(3.2, 30.52) * mm});
            skArc(sketch, "E8.trimOffspring", {"start": v(-11, 28.65) * mm, "mid": v(-11.74, 28.35) * mm, "end": v(-12.48, 28.03) * mm});
            skArc(sketch, "E9.trimOffspring", {"start": v(-13.93, 27.34) * mm, "mid": v(-14.64, 26.96) * mm, "end": v(-15.34, 26.57) * mm});
            skArc(sketch, "E10.trimOffspring", {"start": v(-16.71, 25.73) * mm, "mid": v(-17.38, 25.29) * mm, "end": v(-18.04, 24.82) * mm});
            skArc(sketch, "E11.trimOffspring", {"start": v(-19.3, 23.85) * mm, "mid": v(-19.93, 23.33) * mm, "end": v(-20.53, 22.8) * mm});
            skArc(sketch, "E12.trimOffspring", {"start": v(-21.7, 21.7) * mm, "mid": v(-22.26, 21.12) * mm, "end": v(-22.8, 20.53) * mm});
            skArc(sketch, "E13.trimOffspring", {"start": v(-23.85, 19.3) * mm, "mid": v(-24.34, 18.68) * mm, "end": v(-24.82, 18.04) * mm});
            skArc(sketch, "E14.trimOffspring", {"start": v(-25.73, 16.71) * mm, "mid": v(-26.16, 16.03) * mm, "end": v(-26.57, 15.34) * mm});
            skArc(sketch, "E15.trimOffspring", {"start": v(-27.34, 13.93) * mm, "mid": v(-27.7, 13.2) * mm, "end": v(-28.03, 12.48) * mm});
            skArc(sketch, "E16.trimOffspring", {"start": v(-28.65, 11) * mm, "mid": v(-28.92, 10.24) * mm, "end": v(-29.18, 9.48) * mm});
            skArc(sketch, "E17.trimOffspring", {"start": v(-29.64, 7.94) * mm, "mid": v(-29.84, 7.16) * mm, "end": v(-30.01, 6.38) * mm});
            skArc(sketch, "E18.trimOffspring", {"start": v(-30.64, 1.6) * mm, "mid": v(-30.67, 0.8) * mm, "end": v(-30.68, 0) * mm});
            skArc(sketch, "E19.trimOffspring", {"start": v(-30.3, 4.8) * mm, "mid": v(-30.42, 4) * mm, "end": v(-30.52, 3.2) * mm});
            skArc(sketch, "E20.trimOffspring", {"start": v(-30.64, -1.6) * mm, "mid": v(-30.59, -2.4) * mm, "end": v(-30.52, -3.2) * mm});
            skArc(sketch, "E21.trimOffspring", {"start": v(-30.3, -4.8) * mm, "mid": v(-30.17, -5.6) * mm, "end": v(-30.01, -6.38) * mm});
            skArc(sketch, "E22.trimOffspring", {"start": v(-29.64, -7.94) * mm, "mid": v(-29.42, -8.71) * mm, "end": v(-29.18, -9.48) * mm});
            skArc(sketch, "E23.trimOffspring", {"start": v(-28.65, -11) * mm, "mid": v(-28.35, -11.74) * mm, "end": v(-28.03, -12.48) * mm});
            skArc(sketch, "E24.trimOffspring", {"start": v(-27.34, -13.93) * mm, "mid": v(-26.96, -14.64) * mm, "end": v(-26.57, -15.34) * mm});
            skArc(sketch, "E25.trimOffspring", {"start": v(-4.8, 30.3) * mm, "mid": v(-5.6, 30.17) * mm, "end": v(-6.38, 30.01) * mm});
            skArc(sketch, "E26.trimOffspring", {"start": v(-1.6, 30.64) * mm, "mid": v(-2.4, 30.59) * mm, "end": v(-3.2, 30.52) * mm});
            skArc(sketch, "E27.trimOffspring", {"start": v(1.6, 30.64) * mm, "mid": v(0.8, 30.67) * mm, "end": v(0, 30.68) * mm});
            skArc(sketch, "E28.trimOffspring", {"start": v(4.8, 30.3) * mm, "mid": v(4, 30.42) * mm, "end": v(3.2, 30.52) * mm});
            skArc(sketch, "E29.trimOffspring", {"start": v(7.94, 29.64) * mm, "mid": v(7.16, 29.84) * mm, "end": v(6.38, 30.01) * mm});
            skArc(sketch, "E30.trimOffspring", {"start": v(11, 28.65) * mm, "mid": v(10.24, 28.92) * mm, "end": v(9.48, 29.18) * mm});
            skArc(sketch, "E31.trimOffspring", {"start": v(13.93, 27.34) * mm, "mid": v(13.2, 27.7) * mm, "end": v(12.48, 28.03) * mm});
            skArc(sketch, "E32.trimOffspring", {"start": v(16.71, 25.73) * mm, "mid": v(16.03, 26.16) * mm, "end": v(15.34, 26.57) * mm});
            skArc(sketch, "E33.trimOffspring", {"start": v(19.3, 23.85) * mm, "mid": v(18.68, 24.34) * mm, "end": v(18.04, 24.82) * mm});
            skArc(sketch, "E34.trimOffspring", {"start": v(21.7, 21.7) * mm, "mid": v(21.12, 22.26) * mm, "end": v(20.53, 22.8) * mm});
            skArc(sketch, "E35.trimOffspring", {"start": v(23.85, 19.3) * mm, "mid": v(23.33, 19.93) * mm, "end": v(22.8, 20.53) * mm});
            skArc(sketch, "E36.trimOffspring", {"start": v(25.73, 16.71) * mm, "mid": v(25.29, 17.38) * mm, "end": v(24.82, 18.04) * mm});
            skArc(sketch, "E37.trimOffspring", {"start": v(27.34, 13.93) * mm, "mid": v(26.96, 14.64) * mm, "end": v(26.57, 15.34) * mm});
            skArc(sketch, "E38.trimOffspring", {"start": v(28.65, 11) * mm, "mid": v(28.35, 11.74) * mm, "end": v(28.03, 12.48) * mm});
            skArc(sketch, "E39.trimOffspring", {"start": v(29.64, 7.94) * mm, "mid": v(29.42, 8.71) * mm, "end": v(29.18, 9.48) * mm});
            skArc(sketch, "E40.trimOffspring", {"start": v(30.3, 4.8) * mm, "mid": v(30.17, 5.6) * mm, "end": v(30.01, 6.38) * mm});
            skArc(sketch, "E41.trimOffspring", {"start": v(30.64, 1.6) * mm, "mid": v(30.59, 2.4) * mm, "end": v(30.52, 3.2) * mm});
            skArc(sketch, "E42.trimOffspring", {"start": v(30.64, -1.6) * mm, "mid": v(30.67, -0.8) * mm, "end": v(30.68, 0) * mm});
            skArc(sketch, "E43.trimOffspring", {"start": v(30.3, -4.8) * mm, "mid": v(30.42, -4) * mm, "end": v(30.52, -3.2) * mm});
            skArc(sketch, "E44.trimOffspring", {"start": v(29.64, -7.94) * mm, "mid": v(29.84, -7.16) * mm, "end": v(30.01, -6.38) * mm});
            skArc(sketch, "E45.trimOffspring", {"start": v(28.65, -11) * mm, "mid": v(28.92, -10.24) * mm, "end": v(29.18, -9.48) * mm});
            skArc(sketch, "E46.trimOffspring", {"start": v(27.34, -13.93) * mm, "mid": v(27.7, -13.2) * mm, "end": v(28.03, -12.48) * mm});
            skArc(sketch, "E47.trimOffspring", {"start": v(25.73, -16.71) * mm, "mid": v(26.16, -16.03) * mm, "end": v(26.57, -15.34) * mm});
            skArc(sketch, "E48.trimOffspring", {"start": v(23.85, -19.3) * mm, "mid": v(24.34, -18.68) * mm, "end": v(24.82, -18.04) * mm});
            skArc(sketch, "E49.trimOffspring", {"start": v(21.7, -21.7) * mm, "mid": v(22.26, -21.12) * mm, "end": v(22.8, -20.53) * mm});
            skArc(sketch, "E50.trimOffspring", {"start": v(19.3, -23.85) * mm, "mid": v(19.93, -23.33) * mm, "end": v(20.53, -22.8) * mm});
            skArc(sketch, "E51.trimOffspring", {"start": v(16.71, -25.73) * mm, "mid": v(17.38, -25.29) * mm, "end": v(18.04, -24.82) * mm});
            skArc(sketch, "E52.trimOffspring", {"start": v(13.93, -27.34) * mm, "mid": v(14.64, -26.96) * mm, "end": v(15.34, -26.57) * mm});
            skArc(sketch, "E53.trimOffspring", {"start": v(11, -28.65) * mm, "mid": v(11.74, -28.35) * mm, "end": v(12.48, -28.03) * mm});
            skArc(sketch, "E54.trimOffspring", {"start": v(7.94, -29.64) * mm, "mid": v(8.71, -29.42) * mm, "end": v(9.48, -29.18) * mm});
            skArc(sketch, "E55.trimOffspring", {"start": v(4.8, -30.3) * mm, "mid": v(5.6, -30.17) * mm, "end": v(6.38, -30.01) * mm});
            skArc(sketch, "E56.trimOffspring", {"start": v(1.6, -30.64) * mm, "mid": v(2.4, -30.59) * mm, "end": v(3.2, -30.52) * mm});
            skArc(sketch, "E57.trimOffspring", {"start": v(-1.6, -30.64) * mm, "mid": v(-0.8, -30.67) * mm, "end": v(0, -30.68) * mm});
            skArc(sketch, "E58.trimOffspring", {"start": v(-4.8, -30.3) * mm, "mid": v(-4, -30.42) * mm, "end": v(-3.2, -30.52) * mm});
            skArc(sketch, "E59.trimOffspring", {"start": v(-7.94, -29.64) * mm, "mid": v(-7.16, -29.84) * mm, "end": v(-6.38, -30.01) * mm});
            skArc(sketch, "E60.trimOffspring", {"start": v(-11, -28.65) * mm, "mid": v(-10.24, -28.92) * mm, "end": v(-9.48, -29.18) * mm});
            skArc(sketch, "E61.trimOffspring", {"start": v(-13.93, -27.34) * mm, "mid": v(-13.2, -27.7) * mm, "end": v(-12.48, -28.03) * mm});
            skArc(sketch, "E62.trimOffspring", {"start": v(-16.71, -25.73) * mm, "mid": v(-16.03, -26.16) * mm, "end": v(-15.34, -26.57) * mm});
            skArc(sketch, "E63.trimOffspring", {"start": v(-19.3, -23.85) * mm, "mid": v(-18.68, -24.34) * mm, "end": v(-18.04, -24.82) * mm});
            skArc(sketch, "E64.trimOffspring", {"start": v(-21.7, -21.7) * mm, "mid": v(-21.12, -22.26) * mm, "end": v(-20.53, -22.8) * mm});
            skArc(sketch, "E65.trimOffspring", {"start": v(-23.85, -19.3) * mm, "mid": v(-23.33, -19.93) * mm, "end": v(-22.8, -20.53) * mm});
            skArc(sketch, "E66.trimOffspring", {"start": v(-25.73, -16.71) * mm, "mid": v(-25.29, -17.38) * mm, "end": v(-24.82, -18.04) * mm});
            skLineSegment(sketch, "E67", {"start": v(32.8, 0.6) * mm, "end": v(-27.19, -0.73) * mm});
            skSolve(sketch);
        }
        {
            var Q0;
            Q0=qSketchRegion(id+"F0",true);
            var Q1;
            Q1=makeQuery(id+"F0.imprint","IMPRINT",FACE,{"disambiguationData":[TD([[makeQuery(id+"F0.imprint","IMPRINT",EDGE,{"derivedFrom":sQuery(id+"F0.wireOp",EDGE,"E0")}),1.0]])]});
            extrude(context, id + "F1", {"entities" : qUnion([Q0, Q1]), "depth" : 5 * mm});
        }
        {
            var Q0;
            Q0=makeQuery(id+"F1.opExtrude","CAP_FACE",FACE,{"disambiguationData":[OSD([sQuery(id+"F0.wireOp",EDGE,"E0"),sQuery(id+"F0.wireOp",EDGE,"E1.trimOffspring"),sQuery(id+"F0.wireOp",EDGE,"E2"),sQuery(id+"F0.wireOp",EDGE,"E3"),sQuery(id+"F0.wireOp",EDGE,"E4.MirrorCS"),sQuery(id+"F0.wireOp",EDGE,"E5.MirrorCS"),sQuery(id+"F0.wireOp",EDGE,"E6.MirrorCS"),sQuery(id+"F0.wireOp",EDGE,"E7.1.0"),sQuery(id+"F0.wireOp",EDGE,"E7.1.1"),sQuery(id+"F0.wireOp",EDGE,"E7.1.2"),sQuery(id+"F0.wireOp",EDGE,"E7.1.3"),sQuery(id+"F0.wireOp",EDGE,"E7.1.4"),sQuery(id+"F0.wireOp",EDGE,"E7.1.5"),sQuery(id+"F0.wireOp",EDGE,"E7.2.0"),sQuery(id+"F0.wireOp",EDGE,"E7.2.1"),sQuery(id+"F0.wireOp",EDGE,"E7.2.2"),sQuery(id+"F0.wireOp",EDGE,"E7.2.3"),sQuery(id+"F0.wireOp",EDGE,"E7.2.4"),sQuery(id+"F0.wireOp",EDGE,"E7.2.5"),sQuery(id+"F0.wireOp",EDGE,"E7.3.0"),sQuery(id+"F0.wireOp",EDGE,"E7.3.1"),sQuery(id+"F0.wireOp",EDGE,"E7.3.2"),sQuery(id+"F0.wireOp",EDGE,"E7.3.3"),sQuery(id+"F0.wireOp",EDGE,"E7.3.4"),sQuery(id+"F0.wireOp",EDGE,"E7.3.5"),sQuery(id+"F0.wireOp",EDGE,"E7.4.0"),sQuery(id+"F0.wireOp",EDGE,"E7.4.1"),sQuery(id+"F0.wireOp",EDGE,"E7.4.2"),sQuery(id+"F0.wireOp",EDGE,"E7.4.3"),sQuery(id+"F0.wireOp",EDGE,"E7.4.4"),sQuery(id+"F0.wireOp",EDGE,"E7.4.5"),sQuery(id+"F0.wireOp",EDGE,"E7.5.0"),sQuery(id+"F0.wireOp",EDGE,"E7.5.1"),sQuery(id+"F0.wireOp",EDGE,"E7.5.2"),sQuery(id+"F0.wireOp",EDGE,"E7.5.3"),sQuery(id+"F0.wireOp",EDGE,"E7.5.4"),sQuery(id+"F0.wireOp",EDGE,"E7.5.5"),sQuery(id+"F0.wireOp",EDGE,"E7.6.0"),sQuery(id+"F0.wireOp",EDGE,"E7.6.1"),sQuery(id+"F0.wireOp",EDGE,"E7.6.2"),sQuery(id+"F0.wireOp",EDGE,"E7.6.3"),sQuery(id+"F0.wireOp",EDGE,"E7.6.4"),sQuery(id+"F0.wireOp",EDGE,"E7.6.5"),sQuery(id+"F0.wireOp",EDGE,"E7.7.0"),sQuery(id+"F0.wireOp",EDGE,"E7.7.1"),sQuery(id+"F0.wireOp",EDGE,"E7.7.2"),sQuery(id+"F0.wireOp",EDGE,"E7.7.3"),sQuery(id+"F0.wireOp",EDGE,"E7.7.4"),sQuery(id+"F0.wireOp",EDGE,"E7.7.5"),sQuery(id+"F0.wireOp",EDGE,"E7.8.0"),sQuery(id+"F0.wireOp",EDGE,"E7.8.1"),sQuery(id+"F0.wireOp",EDGE,"E7.8.2"),sQuery(id+"F0.wireOp",EDGE,"E7.8.3"),sQuery(id+"F0.wireOp",EDGE,"E7.8.4"),sQuery(id+"F0.wireOp",EDGE,"E7.8.5"),sQuery(id+"F0.wireOp",EDGE,"E7.9.0"),sQuery(id+"F0.wireOp",EDGE,"E7.9.1"),sQuery(id+"F0.wireOp",EDGE,"E7.9.2"),sQuery(id+"F0.wireOp",EDGE,"E7.9.3"),sQuery(id+"F0.wireOp",EDGE,"E7.9.4"),sQuery(id+"F0.wireOp",EDGE,"E7.9.5"),sQuery(id+"F0.wireOp",EDGE,"E7.10.0"),sQuery(id+"F0.wireOp",EDGE,"E7.10.1"),sQuery(id+"F0.wireOp",EDGE,"E7.10.2"),sQuery(id+"F0.wireOp",EDGE,"E7.10.3"),sQuery(id+"F0.wireOp",EDGE,"E7.10.4"),sQuery(id+"F0.wireOp",EDGE,"E7.10.5"),sQuery(id+"F0.wireOp",EDGE,"E7.11.0"),sQuery(id+"F0.wireOp",EDGE,"E7.11.1"),sQuery(id+"F0.wireOp",EDGE,"E7.11.2"),sQuery(id+"F0.wireOp",EDGE,"E7.11.3"),sQuery(id+"F0.wireOp",EDGE,"E7.11.4"),sQuery(id+"F0.wireOp",EDGE,"E7.11.5"),sQuery(id+"F0.wireOp",EDGE,"E7.12.0"),sQuery(id+"F0.wireOp",EDGE,"E7.12.1"),sQuery(id+"F0.wireOp",EDGE,"E7.12.2"),sQuery(id+"F0.wireOp",EDGE,"E7.12.3"),sQuery(id+"F0.wireOp",EDGE,"E7.12.4"),sQuery(id+"F0.wireOp",EDGE,"E7.12.5"),sQuery(id+"F0.wireOp",EDGE,"E7.13.0"),sQuery(id+"F0.wireOp",EDGE,"E7.13.1"),sQuery(id+"F0.wireOp",EDGE,"E7.13.2"),sQuery(id+"F0.wireOp",EDGE,"E7.13.3"),sQuery(id+"F0.wireOp",EDGE,"E7.13.4"),sQuery(id+"F0.wireOp",EDGE,"E7.13.5"),sQuery(id+"F0.wireOp",EDGE,"E7.14.0"),sQuery(id+"F0.wireOp",EDGE,"E7.14.1"),sQuery(id+"F0.wireOp",EDGE,"E7.14.2"),sQuery(id+"F0.wireOp",EDGE,"E7.14.3"),sQuery(id+"F0.wireOp",EDGE,"E7.14.4"),sQuery(id+"F0.wireOp",EDGE,"E7.14.5"),sQuery(id+"F0.wireOp",EDGE,"E7.15.0"),sQuery(id+"F0.wireOp",EDGE,"E7.15.1"),sQuery(id+"F0.wireOp",EDGE,"E7.15.2"),sQuery(id+"F0.wireOp",EDGE,"E7.15.3"),sQuery(id+"F0.wireOp",EDGE,"E7.15.4"),sQuery(id+"F0.wireOp",EDGE,"E7.15.5"),sQuery(id+"F0.wireOp",EDGE,"E7.16.0"),sQuery(id+"F0.wireOp",EDGE,"E7.16.1"),sQuery(id+"F0.wireOp",EDGE,"E7.16.2"),sQuery(id+"F0.wireOp",EDGE,"E7.16.3"),sQuery(id+"F0.wireOp",EDGE,"E7.16.4"),sQuery(id+"F0.wireOp",EDGE,"E7.16.5"),sQuery(id+"F0.wireOp",EDGE,"E7.17.0"),sQuery(id+"F0.wireOp",EDGE,"E7.17.1"),sQuery(id+"F0.wireOp",EDGE,"E7.17.2"),sQuery(id+"F0.wireOp",EDGE,"E7.17.3"),sQuery(id+"F0.wireOp",EDGE,"E7.17.4"),sQuery(id+"F0.wireOp",EDGE,"E7.17.5"),sQuery(id+"F0.wireOp",EDGE,"E7.18.0"),sQuery(id+"F0.wireOp",EDGE,"E7.18.1"),sQuery(id+"F0.wireOp",EDGE,"E7.18.2"),sQuery(id+"F0.wireOp",EDGE,"E7.18.3"),sQuery(id+"F0.wireOp",EDGE,"E7.18.4"),sQuery(id+"F0.wireOp",EDGE,"E7.18.5"),sQuery(id+"F0.wireOp",EDGE,"E7.19.0"),sQuery(id+"F0.wireOp",EDGE,"E7.19.1"),sQuery(id+"F0.wireOp",EDGE,"E7.19.2"),sQuery(id+"F0.wireOp",EDGE,"E7.19.3"),sQuery(id+"F0.wireOp",EDGE,"E7.19.4"),sQuery(id+"F0.wireOp",EDGE,"E7.19.5"),sQuery(id+"F0.wireOp",EDGE,"E7.20.0"),sQuery(id+"F0.wireOp",EDGE,"E7.20.1"),sQuery(id+"F0.wireOp",EDGE,"E7.20.2"),sQuery(id+"F0.wireOp",EDGE,"E7.20.3"),sQuery(id+"F0.wireOp",EDGE,"E7.20.4"),sQuery(id+"F0.wireOp",EDGE,"E7.20.5"),sQuery(id+"F0.wireOp",EDGE,"E7.21.0"),sQuery(id+"F0.wireOp",EDGE,"E7.21.1"),sQuery(id+"F0.wireOp",EDGE,"E7.21.2"),sQuery(id+"F0.wireOp",EDGE,"E7.21.3"),sQuery(id+"F0.wireOp",EDGE,"E7.21.4"),sQuery(id+"F0.wireOp",EDGE,"E7.21.5"),sQuery(id+"F0.wireOp",EDGE,"E7.22.0"),sQuery(id+"F0.wireOp",EDGE,"E7.22.1"),sQuery(id+"F0.wireOp",EDGE,"E7.22.2"),sQuery(id+"F0.wireOp",EDGE,"E7.22.3"),sQuery(id+"F0.wireOp",EDGE,"E7.22.4"),sQuery(id+"F0.wireOp",EDGE,"E7.22.5"),sQuery(id+"F0.wireOp",EDGE,"E7.23.0"),sQuery(id+"F0.wireOp",EDGE,"E7.23.1"),sQuery(id+"F0.wireOp",EDGE,"E7.23.2"),sQuery(id+"F0.wireOp",EDGE,"E7.23.3"),sQuery(id+"F0.wireOp",EDGE,"E7.23.4"),sQuery(id+"F0.wireOp",EDGE,"E7.23.5"),sQuery(id+"F0.wireOp",EDGE,"E7.24.0"),sQuery(id+"F0.wireOp",EDGE,"E7.24.1"),sQuery(id+"F0.wireOp",EDGE,"E7.24.2"),sQuery(id+"F0.wireOp",EDGE,"E7.24.3"),sQuery(id+"F0.wireOp",EDGE,"E7.24.4"),sQuery(id+"F0.wireOp",EDGE,"E7.24.5"),sQuery(id+"F0.wireOp",EDGE,"E7.25.0"),sQuery(id+"F0.wireOp",EDGE,"E7.25.1"),sQuery(id+"F0.wireOp",EDGE,"E7.25.2"),sQuery(id+"F0.wireOp",EDGE,"E7.25.3"),sQuery(id+"F0.wireOp",EDGE,"E7.25.4"),sQuery(id+"F0.wireOp",EDGE,"E7.25.5"),sQuery(id+"F0.wireOp",EDGE,"E7.26.0"),sQuery(id+"F0.wireOp",EDGE,"E7.26.1"),sQuery(id+"F0.wireOp",EDGE,"E7.26.2"),sQuery(id+"F0.wireOp",EDGE,"E7.26.3"),sQuery(id+"F0.wireOp",EDGE,"E7.26.4"),sQuery(id+"F0.wireOp",EDGE,"E7.26.5"),sQuery(id+"F0.wireOp",EDGE,"E7.27.0"),sQuery(id+"F0.wireOp",EDGE,"E7.27.1"),sQuery(id+"F0.wireOp",EDGE,"E7.27.2"),sQuery(id+"F0.wireOp",EDGE,"E7.27.3"),sQuery(id+"F0.wireOp",EDGE,"E7.27.4"),sQuery(id+"F0.wireOp",EDGE,"E7.27.5"),sQuery(id+"F0.wireOp",EDGE,"E7.28.0"),sQuery(id+"F0.wireOp",EDGE,"E7.28.1"),sQuery(id+"F0.wireOp",EDGE,"E7.28.2"),sQuery(id+"F0.wireOp",EDGE,"E7.28.3"),sQuery(id+"F0.wireOp",EDGE,"E7.28.4"),sQuery(id+"F0.wireOp",EDGE,"E7.28.5"),sQuery(id+"F0.wireOp",EDGE,"E7.29.0"),sQuery(id+"F0.wireOp",EDGE,"E7.29.1"),sQuery(id+"F0.wireOp",EDGE,"E7.29.2"),sQuery(id+"F0.wireOp",EDGE,"E7.29.3"),sQuery(id+"F0.wireOp",EDGE,"E7.29.4"),sQuery(id+"F0.wireOp",EDGE,"E7.29.5"),sQuery(id+"F0.wireOp",EDGE,"E7.30.0"),sQuery(id+"F0.wireOp",EDGE,"E7.30.1"),sQuery(id+"F0.wireOp",EDGE,"E7.30.2"),sQuery(id+"F0.wireOp",EDGE,"E7.30.3"),sQuery(id+"F0.wireOp",EDGE,"E7.30.4"),sQuery(id+"F0.wireOp",EDGE,"E7.30.5"),sQuery(id+"F0.wireOp",EDGE,"E7.31.0"),sQuery(id+"F0.wireOp",EDGE,"E7.31.1"),sQuery(id+"F0.wireOp",EDGE,"E7.31.2"),sQuery(id+"F0.wireOp",EDGE,"E7.31.3"),sQuery(id+"F0.wireOp",EDGE,"E7.31.4"),sQuery(id+"F0.wireOp",EDGE,"E7.31.5"),sQuery(id+"F0.wireOp",EDGE,"E7.32.0"),sQuery(id+"F0.wireOp",EDGE,"E7.32.1"),sQuery(id+"F0.wireOp",EDGE,"E7.32.2"),sQuery(id+"F0.wireOp",EDGE,"E7.32.3"),sQuery(id+"F0.wireOp",EDGE,"E7.32.4"),sQuery(id+"F0.wireOp",EDGE,"E7.32.5"),sQuery(id+"F0.wireOp",EDGE,"E7.33.0"),sQuery(id+"F0.wireOp",EDGE,"E7.33.1"),sQuery(id+"F0.wireOp",EDGE,"E7.33.2"),sQuery(id+"F0.wireOp",EDGE,"E7.33.3"),sQuery(id+"F0.wireOp",EDGE,"E7.33.4"),sQuery(id+"F0.wireOp",EDGE,"E7.33.5"),sQuery(id+"F0.wireOp",EDGE,"E7.34.0"),sQuery(id+"F0.wireOp",EDGE,"E7.34.1"),sQuery(id+"F0.wireOp",EDGE,"E7.34.2"),sQuery(id+"F0.wireOp",EDGE,"E7.34.3"),sQuery(id+"F0.wireOp",EDGE,"E7.34.4"),sQuery(id+"F0.wireOp",EDGE,"E7.34.5"),sQuery(id+"F0.wireOp",EDGE,"E7.35.0"),sQuery(id+"F0.wireOp",EDGE,"E7.35.1"),sQuery(id+"F0.wireOp",EDGE,"E7.35.2"),sQuery(id+"F0.wireOp",EDGE,"E7.35.3"),sQuery(id+"F0.wireOp",EDGE,"E7.35.4"),sQuery(id+"F0.wireOp",EDGE,"E7.35.5"),sQuery(id+"F0.wireOp",EDGE,"E7.36.0"),sQuery(id+"F0.wireOp",EDGE,"E7.36.1"),sQuery(id+"F0.wireOp",EDGE,"E7.36.2"),sQuery(id+"F0.wireOp",EDGE,"E7.36.3"),sQuery(id+"F0.wireOp",EDGE,"E7.36.4"),sQuery(id+"F0.wireOp",EDGE,"E7.36.5"),sQuery(id+"F0.wireOp",EDGE,"E7.37.0"),sQuery(id+"F0.wireOp",EDGE,"E7.37.1"),sQuery(id+"F0.wireOp",EDGE,"E7.37.2"),sQuery(id+"F0.wireOp",EDGE,"E7.37.3"),sQuery(id+"F0.wireOp",EDGE,"E7.37.4"),sQuery(id+"F0.wireOp",EDGE,"E7.37.5"),sQuery(id+"F0.wireOp",EDGE,"E7.38.0"),sQuery(id+"F0.wireOp",EDGE,"E7.38.1"),sQuery(id+"F0.wireOp",EDGE,"E7.38.2"),sQuery(id+"F0.wireOp",EDGE,"E7.38.3"),sQuery(id+"F0.wireOp",EDGE,"E7.38.4"),sQuery(id+"F0.wireOp",EDGE,"E7.38.5"),sQuery(id+"F0.wireOp",EDGE,"E7.39.0"),sQuery(id+"F0.wireOp",EDGE,"E7.39.1"),sQuery(id+"F0.wireOp",EDGE,"E7.39.2"),sQuery(id+"F0.wireOp",EDGE,"E7.39.3"),sQuery(id+"F0.wireOp",EDGE,"E7.39.4"),sQuery(id+"F0.wireOp",EDGE,"E7.39.5"),sQuery(id+"F0.wireOp",EDGE,"E7.40.0"),sQuery(id+"F0.wireOp",EDGE,"E7.40.1"),sQuery(id+"F0.wireOp",EDGE,"E7.40.2"),sQuery(id+"F0.wireOp",EDGE,"E7.40.3"),sQuery(id+"F0.wireOp",EDGE,"E7.40.4"),sQuery(id+"F0.wireOp",EDGE,"E7.40.5"),sQuery(id+"F0.wireOp",EDGE,"E7.41.0"),sQuery(id+"F0.wireOp",EDGE,"E7.41.1"),sQuery(id+"F0.wireOp",EDGE,"E7.41.2"),sQuery(id+"F0.wireOp",EDGE,"E7.41.3"),sQuery(id+"F0.wireOp",EDGE,"E7.41.4"),sQuery(id+"F0.wireOp",EDGE,"E7.41.5"),sQuery(id+"F0.wireOp",EDGE,"E7.42.0"),sQuery(id+"F0.wireOp",EDGE,"E7.42.1"),sQuery(id+"F0.wireOp",EDGE,"E7.42.2"),sQuery(id+"F0.wireOp",EDGE,"E7.42.3"),sQuery(id+"F0.wireOp",EDGE,"E7.42.4"),sQuery(id+"F0.wireOp",EDGE,"E7.42.5"),sQuery(id+"F0.wireOp",EDGE,"E7.43.0"),sQuery(id+"F0.wireOp",EDGE,"E7.43.1"),sQuery(id+"F0.wireOp",EDGE,"E7.43.2"),sQuery(id+"F0.wireOp",EDGE,"E7.43.3"),sQuery(id+"F0.wireOp",EDGE,"E7.43.4"),sQuery(id+"F0.wireOp",EDGE,"E7.43.5"),sQuery(id+"F0.wireOp",EDGE,"E7.44.0"),sQuery(id+"F0.wireOp",EDGE,"E7.44.1"),sQuery(id+"F0.wireOp",EDGE,"E7.44.2"),sQuery(id+"F0.wireOp",EDGE,"E7.44.3"),sQuery(id+"F0.wireOp",EDGE,"E7.44.4"),sQuery(id+"F0.wireOp",EDGE,"E7.44.5"),sQuery(id+"F0.wireOp",EDGE,"E7.45.0"),sQuery(id+"F0.wireOp",EDGE,"E7.45.1"),sQuery(id+"F0.wireOp",EDGE,"E7.45.2"),sQuery(id+"F0.wireOp",EDGE,"E7.45.3"),sQuery(id+"F0.wireOp",EDGE,"E7.45.4"),sQuery(id+"F0.wireOp",EDGE,"E7.45.5"),sQuery(id+"F0.wireOp",EDGE,"E7.46.0"),sQuery(id+"F0.wireOp",EDGE,"E7.46.1"),sQuery(id+"F0.wireOp",EDGE,"E7.46.2"),sQuery(id+"F0.wireOp",EDGE,"E7.46.3"),sQuery(id+"F0.wireOp",EDGE,"E7.46.4"),sQuery(id+"F0.wireOp",EDGE,"E7.46.5"),sQuery(id+"F0.wireOp",EDGE,"E7.47.0"),sQuery(id+"F0.wireOp",EDGE,"E7.47.1"),sQuery(id+"F0.wireOp",EDGE,"E7.47.2"),sQuery(id+"F0.wireOp",EDGE,"E7.47.3"),sQuery(id+"F0.wireOp",EDGE,"E7.47.4"),sQuery(id+"F0.wireOp",EDGE,"E7.47.5"),sQuery(id+"F0.wireOp",EDGE,"E7.48.0"),sQuery(id+"F0.wireOp",EDGE,"E7.48.1"),sQuery(id+"F0.wireOp",EDGE,"E7.48.2"),sQuery(id+"F0.wireOp",EDGE,"E7.48.3"),sQuery(id+"F0.wireOp",EDGE,"E7.48.4"),sQuery(id+"F0.wireOp",EDGE,"E7.48.5"),sQuery(id+"F0.wireOp",EDGE,"E7.49.0"),sQuery(id+"F0.wireOp",EDGE,"E7.49.1"),sQuery(id+"F0.wireOp",EDGE,"E7.49.2"),sQuery(id+"F0.wireOp",EDGE,"E7.49.3"),sQuery(id+"F0.wireOp",EDGE,"E7.49.4"),sQuery(id+"F0.wireOp",EDGE,"E7.49.5"),sQuery(id+"F0.wireOp",EDGE,"E7.50.0"),sQuery(id+"F0.wireOp",EDGE,"E7.50.1"),sQuery(id+"F0.wireOp",EDGE,"E7.50.2"),sQuery(id+"F0.wireOp",EDGE,"E7.50.3"),sQuery(id+"F0.wireOp",EDGE,"E7.50.4"),sQuery(id+"F0.wireOp",EDGE,"E7.50.5"),sQuery(id+"F0.wireOp",EDGE,"E7.51.0"),sQuery(id+"F0.wireOp",EDGE,"E7.51.1"),sQuery(id+"F0.wireOp",EDGE,"E7.51.2"),sQuery(id+"F0.wireOp",EDGE,"E7.51.3"),sQuery(id+"F0.wireOp",EDGE,"E7.51.4"),sQuery(id+"F0.wireOp",EDGE,"E7.51.5"),sQuery(id+"F0.wireOp",EDGE,"E7.52.0"),sQuery(id+"F0.wireOp",EDGE,"E7.52.1"),sQuery(id+"F0.wireOp",EDGE,"E7.52.2"),sQuery(id+"F0.wireOp",EDGE,"E7.52.3"),sQuery(id+"F0.wireOp",EDGE,"E7.52.4"),sQuery(id+"F0.wireOp",EDGE,"E7.52.5"),sQuery(id+"F0.wireOp",EDGE,"E7.53.0"),sQuery(id+"F0.wireOp",EDGE,"E7.53.1"),sQuery(id+"F0.wireOp",EDGE,"E7.53.2"),sQuery(id+"F0.wireOp",EDGE,"E7.53.3"),sQuery(id+"F0.wireOp",EDGE,"E7.53.4"),sQuery(id+"F0.wireOp",EDGE,"E7.53.5"),sQuery(id+"F0.wireOp",EDGE,"E7.54.0"),sQuery(id+"F0.wireOp",EDGE,"E7.54.1"),sQuery(id+"F0.wireOp",EDGE,"E7.54.2"),sQuery(id+"F0.wireOp",EDGE,"E7.54.3"),sQuery(id+"F0.wireOp",EDGE,"E7.54.4"),sQuery(id+"F0.wireOp",EDGE,"E7.54.5"),sQuery(id+"F0.wireOp",EDGE,"E7.55.0"),sQuery(id+"F0.wireOp",EDGE,"E7.55.1"),sQuery(id+"F0.wireOp",EDGE,"E7.55.2"),sQuery(id+"F0.wireOp",EDGE,"E7.55.3"),sQuery(id+"F0.wireOp",EDGE,"E7.55.4"),sQuery(id+"F0.wireOp",EDGE,"E7.55.5"),sQuery(id+"F0.wireOp",EDGE,"E7.56.0"),sQuery(id+"F0.wireOp",EDGE,"E7.56.1"),sQuery(id+"F0.wireOp",EDGE,"E7.56.2"),sQuery(id+"F0.wireOp",EDGE,"E7.56.3"),sQuery(id+"F0.wireOp",EDGE,"E7.56.4"),sQuery(id+"F0.wireOp",EDGE,"E7.56.5"),sQuery(id+"F0.wireOp",EDGE,"E7.57.0"),sQuery(id+"F0.wireOp",EDGE,"E7.57.1"),sQuery(id+"F0.wireOp",EDGE,"E7.57.2"),sQuery(id+"F0.wireOp",EDGE,"E7.57.3"),sQuery(id+"F0.wireOp",EDGE,"E7.57.4"),sQuery(id+"F0.wireOp",EDGE,"E7.57.5"),sQuery(id+"F0.wireOp",EDGE,"E7.58.0"),sQuery(id+"F0.wireOp",EDGE,"E7.58.1"),sQuery(id+"F0.wireOp",EDGE,"E7.58.2"),sQuery(id+"F0.wireOp",EDGE,"E7.58.3"),sQuery(id+"F0.wireOp",EDGE,"E7.58.4"),sQuery(id+"F0.wireOp",EDGE,"E7.58.5"),sQuery(id+"F0.wireOp",EDGE,"E7.59.0"),sQuery(id+"F0.wireOp",EDGE,"E7.59.1"),sQuery(id+"F0.wireOp",EDGE,"E7.59.2"),sQuery(id+"F0.wireOp",EDGE,"E7.59.3"),sQuery(id+"F0.wireOp",EDGE,"E7.59.4"),sQuery(id+"F0.wireOp",EDGE,"E7.59.5"),sQuery(id+"F0.wireOp",EDGE,"E8.trimOffspring"),sQuery(id+"F0.wireOp",EDGE,"E9.trimOffspring"),sQuery(id+"F0.wireOp",EDGE,"E10.trimOffspring"),sQuery(id+"F0.wireOp",EDGE,"E11.trimOffspring"),sQuery(id+"F0.wireOp",EDGE,"E12.trimOffspring"),sQuery(id+"F0.wireOp",EDGE,"E13.trimOffspring"),sQuery(id+"F0.wireOp",EDGE,"E14.trimOffspring"),sQuery(id+"F0.wireOp",EDGE,"E15.trimOffspring"),sQuery(id+"F0.wireOp",EDGE,"E16.trimOffspring"),sQuery(id+"F0.wireOp",EDGE,"E17.trimOffspring"),sQuery(id+"F0.wireOp",EDGE,"E18.trimOffspring"),sQuery(id+"F0.wireOp",EDGE,"E19.trimOffspring"),sQuery(id+"F0.wireOp",EDGE,"E20.trimOffspring"),sQuery(id+"F0.wireOp",EDGE,"E21.trimOffspring"),sQuery(id+"F0.wireOp",EDGE,"E22.trimOffspring"),sQuery(id+"F0.wireOp",EDGE,"E23.trimOffspring"),sQuery(id+"F0.wireOp",EDGE,"E24.trimOffspring"),sQuery(id+"F0.wireOp",EDGE,"E25.trimOffspring"),sQuery(id+"F0.wireOp",EDGE,"E26.trimOffspring"),sQuery(id+"F0.wireOp",EDGE,"E27.trimOffspring"),sQuery(id+"F0.wireOp",EDGE,"E28.trimOffspring"),sQuery(id+"F0.wireOp",EDGE,"E29.trimOffspring"),sQuery(id+"F0.wireOp",EDGE,"E30.trimOffspring"),sQuery(id+"F0.wireOp",EDGE,"E31.trimOffspring"),sQuery(id+"F0.wireOp",EDGE,"E32.trimOffspring"),sQuery(id+"F0.wireOp",EDGE,"E33.trimOffspring"),sQuery(id+"F0.wireOp",EDGE,"E34.trimOffspring"),sQuery(id+"F0.wireOp",EDGE,"E35.trimOffspring"),sQuery(id+"F0.wireOp",EDGE,"E36.trimOffspring"),sQuery(id+"F0.wireOp",EDGE,"E37.trimOffspring"),sQuery(id+"F0.wireOp",EDGE,"E38.trimOffspring"),sQuery(id+"F0.wireOp",EDGE,"E39.trimOffspring"),sQuery(id+"F0.wireOp",EDGE,"E40.trimOffspring"),sQuery(id+"F0.wireOp",EDGE,"E41.trimOffspring"),sQuery(id+"F0.wireOp",EDGE,"E42.trimOffspring"),sQuery(id+"F0.wireOp",EDGE,"E43.trimOffspring"),sQuery(id+"F0.wireOp",EDGE,"E44.trimOffspring"),sQuery(id+"F0.wireOp",EDGE,"E45.trimOffspring"),sQuery(id+"F0.wireOp",EDGE,"E46.trimOffspring"),sQuery(id+"F0.wireOp",EDGE,"E47.trimOffspring"),sQuery(id+"F0.wireOp",EDGE,"E48.trimOffspring"),sQuery(id+"F0.wireOp",EDGE,"E49.trimOffspring"),sQuery(id+"F0.wireOp",EDGE,"E50.trimOffspring"),sQuery(id+"F0.wireOp",EDGE,"E51.trimOffspring"),sQuery(id+"F0.wireOp",EDGE,"E52.trimOffspring"),sQuery(id+"F0.wireOp",EDGE,"E53.trimOffspring"),sQuery(id+"F0.wireOp",EDGE,"E54.trimOffspring"),sQuery(id+"F0.wireOp",EDGE,"E55.trimOffspring"),sQuery(id+"F0.wireOp",EDGE,"E56.trimOffspring"),sQuery(id+"F0.wireOp",EDGE,"E57.trimOffspring"),sQuery(id+"F0.wireOp",EDGE,"E58.trimOffspring"),sQuery(id+"F0.wireOp",EDGE,"E59.trimOffspring"),sQuery(id+"F0.wireOp",EDGE,"E60.trimOffspring"),sQuery(id+"F0.wireOp",EDGE,"E61.trimOffspring"),sQuery(id+"F0.wireOp",EDGE,"E62.trimOffspring"),sQuery(id+"F0.wireOp",EDGE,"E63.trimOffspring"),sQuery(id+"F0.wireOp",EDGE,"E64.trimOffspring"),sQuery(id+"F0.wireOp",EDGE,"E65.trimOffspring"),sQuery(id+"F0.wireOp",EDGE,"E66.trimOffspring")])],"isStart":false});
            var sketch = newSketch(context, id + "F2", { "sketchPlane" : qUnion([Q0])});
            skCircle(sketch, "E68", {"center": v(0, 0) * mm, "radius": 1.78 * mm});
            skSolve(sketch);
        }
        {
            var Q0;
            Q0=qSketchRegion(id+"F2",true);
            extrude(context, id + "F3", {"entities" : qUnion([Q0]), "operationType" : NewBodyOperationType.REMOVE, "oppositeDirection" : true, "depth" : 25.4 * mm});
        }
    });
